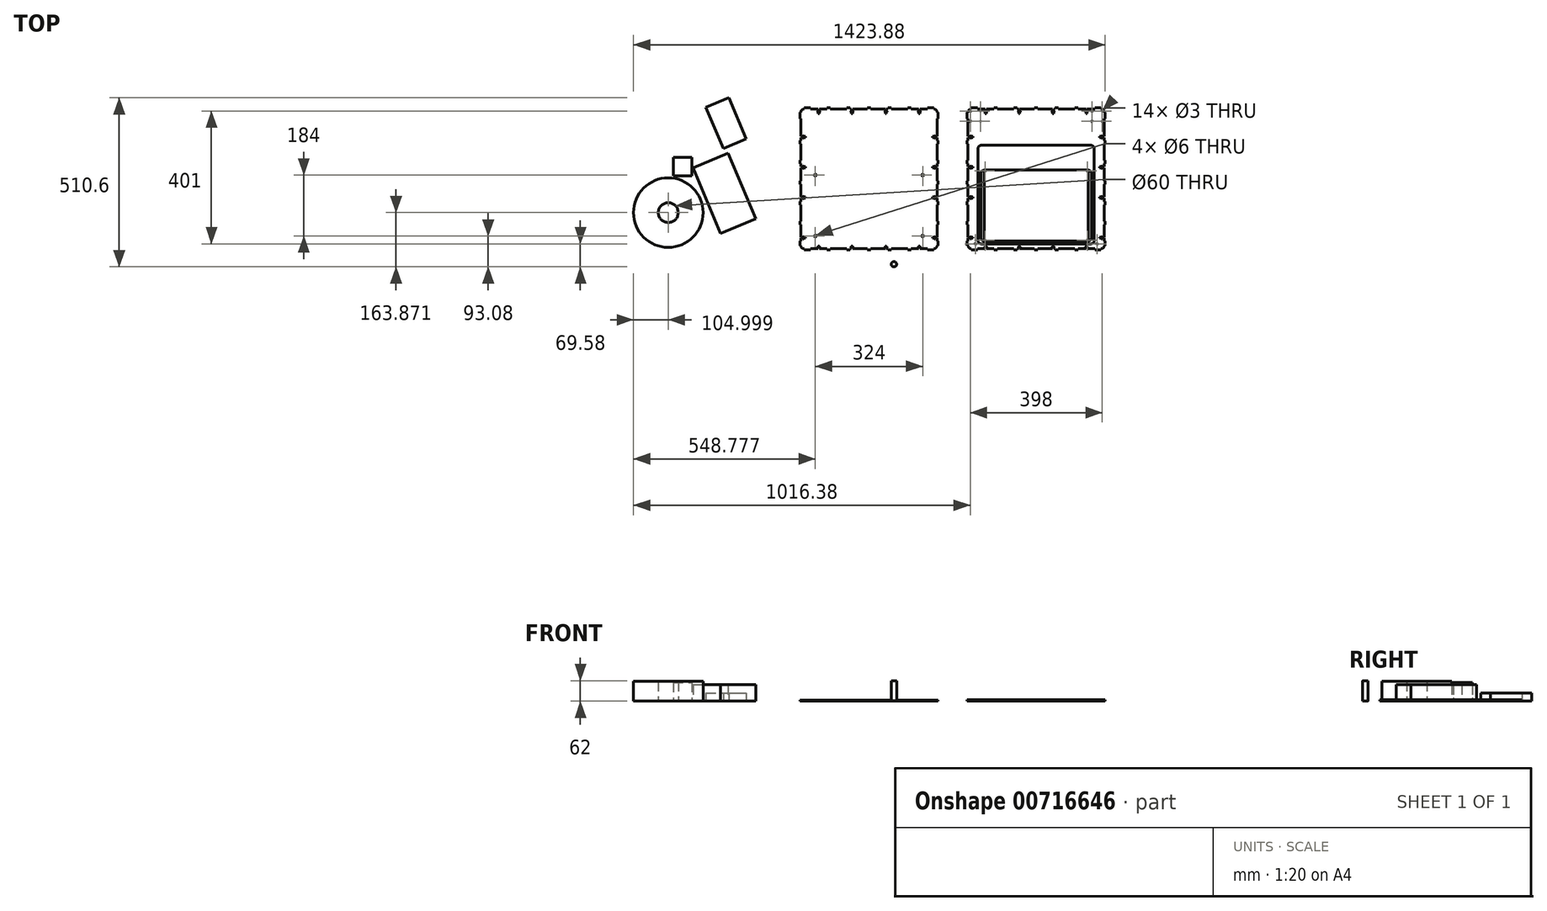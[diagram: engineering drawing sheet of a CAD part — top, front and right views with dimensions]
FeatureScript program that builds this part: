
annotation { "Feature Type Name" : "Feature", "Feature Type Description" : "" }
export const myFeature = defineFeature(function(context is Context, id is Id, definition is map)
    precondition{}
    {
        {
            var Q0;
            Q0=qCreatedBy(makeId("Top.planeOp"),FACE);
            var sketch = newSketch(context, id + "F0", { "sketchPlane" : qUnion([Q0])});
            skCircle(sketch, "E0", {"center": v(-429.2, -257.83) * mm, "radius": 8 * mm});
            skSolve(sketch);
        }
        {
            var Q0;
            Q0=makeQuery(id+"F0.imprint","IMPRINT",FACE,{"disambiguationData":[TD([[makeQuery(id+"F0.imprint","IMPRINT",EDGE,{"derivedFrom":sQuery(id+"F0.wireOp",EDGE,"E0")}),1.0]])]});
            extrude(context, id + "F1", {"entities" : qUnion([Q0]), "depth" : 62 * mm, "offsetDistance" : 25 * mm});
        }
        {
            var Q0;
            Q0=qCreatedBy(makeId("Top.planeOp"),FACE);
            var sketch = newSketch(context, id + "F2", { "sketchPlane" : qUnion([Q0])});
            skLineSegment(sketch, "E1", {"start": v(49.3, -211.25) * mm, "end": v(5, -211.25) * mm});
            skLineSegment(sketch, "E2", {"start": v(49.3, -208.35) * mm, "end": v(49.3, -211.25) * mm});
            skLineSegment(sketch, "E3", {"start": v(49.3, -208.35) * mm, "end": v(47.8, -208.35) * mm});
            skLineSegment(sketch, "E4", {"start": v(47.8, -205.75) * mm, "end": v(47.8, -208.35) * mm});
            skLineSegment(sketch, "E5", {"start": v(49.3, -205.75) * mm, "end": v(47.8, -205.75) * mm});
            skLineSegment(sketch, "E6", {"start": v(49.3, -202.75) * mm, "end": v(49.3, -205.75) * mm});
            skLineSegment(sketch, "E7", {"start": v(52.7, -202.75) * mm, "end": v(49.3, -202.75) * mm});
            skLineSegment(sketch, "E8", {"start": v(52.7, -205.75) * mm, "end": v(52.7, -202.75) * mm});
            skLineSegment(sketch, "E9", {"start": v(54.2, -205.75) * mm, "end": v(52.7, -205.75) * mm});
            skLineSegment(sketch, "E10", {"start": v(54.2, -208.35) * mm, "end": v(54.2, -205.75) * mm});
            skLineSegment(sketch, "E11", {"start": v(54.2, -208.35) * mm, "end": v(52.7, -208.35) * mm});
            skLineSegment(sketch, "E12", {"start": v(52.7, -211.25) * mm, "end": v(52.7, -208.35) * mm});
            skLineSegment(sketch, "E13", {"start": v(57, -211.25) * mm, "end": v(52.7, -211.25) * mm});
            skLineSegment(sketch, "E14", {"start": v(57, -214.25) * mm, "end": v(57, -211.25) * mm});
            skLineSegment(sketch, "E15", {"start": v(67, -214.25) * mm, "end": v(57, -214.25) * mm});
            skLineSegment(sketch, "E16", {"start": v(67, -211.25) * mm, "end": v(67, -214.25) * mm});
            skLineSegment(sketch, "E17", {"start": v(117, -211.25) * mm, "end": v(67, -211.25) * mm});
            skLineSegment(sketch, "E18", {"start": v(117, -214.25) * mm, "end": v(117, -211.25) * mm});
            skLineSegment(sketch, "E19", {"start": v(127, -214.25) * mm, "end": v(117, -214.25) * mm});
            skLineSegment(sketch, "E20", {"start": v(127, -211.25) * mm, "end": v(127, -214.25) * mm});
            skLineSegment(sketch, "E21", {"start": v(150.3, -211.25) * mm, "end": v(127, -211.25) * mm});
            skLineSegment(sketch, "E22", {"start": v(150.3, -208.35) * mm, "end": v(150.3, -211.25) * mm});
            skLineSegment(sketch, "E23", {"start": v(148.8, -208.35) * mm, "end": v(150.3, -208.35) * mm});
            skLineSegment(sketch, "E24", {"start": v(148.8, -205.75) * mm, "end": v(148.8, -208.35) * mm});
            skLineSegment(sketch, "E25", {"start": v(150.3, -205.75) * mm, "end": v(148.8, -205.75) * mm});
            skLineSegment(sketch, "E26", {"start": v(150.3, -202.75) * mm, "end": v(150.3, -205.75) * mm});
            skLineSegment(sketch, "E27", {"start": v(153.7, -202.75) * mm, "end": v(150.3, -202.75) * mm});
            skLineSegment(sketch, "E28", {"start": v(153.7, -205.75) * mm, "end": v(153.7, -202.75) * mm});
            skLineSegment(sketch, "E29", {"start": v(155.2, -205.75) * mm, "end": v(153.7, -205.75) * mm});
            skLineSegment(sketch, "E30", {"start": v(155.2, -208.35) * mm, "end": v(155.2, -205.75) * mm});
            skLineSegment(sketch, "E31", {"start": v(153.7, -208.35) * mm, "end": v(155.2, -208.35) * mm});
            skLineSegment(sketch, "E32", {"start": v(153.7, -211.25) * mm, "end": v(153.7, -208.35) * mm});
            skLineSegment(sketch, "E33", {"start": v(177, -211.25) * mm, "end": v(153.7, -211.25) * mm});
            skLineSegment(sketch, "E34", {"start": v(177, -214.25) * mm, "end": v(177, -211.25) * mm});
            skLineSegment(sketch, "E35", {"start": v(195.5, -214.25) * mm, "end": v(177, -214.25) * mm});
            skLineSegment(sketch, "E36", {"start": v(195.5, -211.25) * mm, "end": v(195.5, -214.25) * mm});
            skArc(sketch, "E37", {"start": v(205.5, -201.25) * mm, "mid": v(202.57, -208.32) * mm, "end": v(195.5, -211.25) * mm});
            skLineSegment(sketch, "E38", {"start": v(208.5, -201.25) * mm, "end": v(205.5, -201.25) * mm});
            skLineSegment(sketch, "E39", {"start": v(208.5, -188.25) * mm, "end": v(208.5, -201.25) * mm});
            skLineSegment(sketch, "E40", {"start": v(205.5, -188.25) * mm, "end": v(208.5, -188.25) * mm});
            skLineSegment(sketch, "E41", {"start": v(205.5, -179.45) * mm, "end": v(205.5, -188.25) * mm});
            skLineSegment(sketch, "E42", {"start": v(199.1, -179.45) * mm, "end": v(205.5, -179.45) * mm});
            skLineSegment(sketch, "E43", {"start": v(199.1, -180.95) * mm, "end": v(199.1, -179.45) * mm});
            skLineSegment(sketch, "E44", {"start": v(196.5, -180.95) * mm, "end": v(199.1, -180.95) * mm});
            skLineSegment(sketch, "E45", {"start": v(196.5, -179.45) * mm, "end": v(196.5, -180.95) * mm});
            skLineSegment(sketch, "E46", {"start": v(191.5, -179.45) * mm, "end": v(196.5, -179.45) * mm});
            skLineSegment(sketch, "E47", {"start": v(191.5, -176.05) * mm, "end": v(191.5, -179.45) * mm});
            skLineSegment(sketch, "E48", {"start": v(196.5, -176.05) * mm, "end": v(191.5, -176.05) * mm});
            skLineSegment(sketch, "E49", {"start": v(196.5, -174.55) * mm, "end": v(196.5, -176.05) * mm});
            skLineSegment(sketch, "E50", {"start": v(199.1, -174.55) * mm, "end": v(196.5, -174.55) * mm});
            skLineSegment(sketch, "E51", {"start": v(199.1, -176.05) * mm, "end": v(199.1, -174.55) * mm});
            skLineSegment(sketch, "E52", {"start": v(205.5, -176.05) * mm, "end": v(199.1, -176.05) * mm});
            skLineSegment(sketch, "E53", {"start": v(205.5, -138.25) * mm, "end": v(205.5, -176.05) * mm});
            skLineSegment(sketch, "E54", {"start": v(208.5, -138.25) * mm, "end": v(205.5, -138.25) * mm});
            skLineSegment(sketch, "E55", {"start": v(208.5, -128.25) * mm, "end": v(208.5, -138.25) * mm});
            skLineSegment(sketch, "E56", {"start": v(205.5, -128.25) * mm, "end": v(208.5, -128.25) * mm});
            skLineSegment(sketch, "E57", {"start": v(205.5, -78.25) * mm, "end": v(205.5, -128.25) * mm});
            skLineSegment(sketch, "E58", {"start": v(208.5, -78.25) * mm, "end": v(205.5, -78.25) * mm});
            skLineSegment(sketch, "E59", {"start": v(208.5, -68.25) * mm, "end": v(208.5, -78.25) * mm});
            skLineSegment(sketch, "E60", {"start": v(205.5, -68.25) * mm, "end": v(208.5, -68.25) * mm});
            skLineSegment(sketch, "E61", {"start": v(205.5, -58.45) * mm, "end": v(205.5, -68.25) * mm});
            skLineSegment(sketch, "E62", {"start": v(199.1, -58.45) * mm, "end": v(205.5, -58.45) * mm});
            skLineSegment(sketch, "E63", {"start": v(199.1, -59.95) * mm, "end": v(199.1, -58.45) * mm});
            skLineSegment(sketch, "E64", {"start": v(196.5, -59.95) * mm, "end": v(199.1, -59.95) * mm});
            skLineSegment(sketch, "E65", {"start": v(196.5, -58.45) * mm, "end": v(196.5, -59.95) * mm});
            skLineSegment(sketch, "E66", {"start": v(191.5, -58.45) * mm, "end": v(196.5, -58.45) * mm});
            skLineSegment(sketch, "E67", {"start": v(191.5, -55.05) * mm, "end": v(191.5, -58.45) * mm});
            skLineSegment(sketch, "E68", {"start": v(196.5, -55.05) * mm, "end": v(191.5, -55.05) * mm});
            skLineSegment(sketch, "E69", {"start": v(196.5, -53.55) * mm, "end": v(196.5, -55.05) * mm});
            skLineSegment(sketch, "E70", {"start": v(199.1, -53.55) * mm, "end": v(196.5, -53.55) * mm});
            skLineSegment(sketch, "E71", {"start": v(199.1, -55.05) * mm, "end": v(199.1, -53.55) * mm});
            skLineSegment(sketch, "E72", {"start": v(205.5, -55.05) * mm, "end": v(199.1, -55.05) * mm});
            skLineSegment(sketch, "E73", {"start": v(205.5, -16.25) * mm, "end": v(205.5, -55.05) * mm});
            skLineSegment(sketch, "E74", {"start": v(208.5, -16.25) * mm, "end": v(205.5, -16.25) * mm});
            skLineSegment(sketch, "E75", {"start": v(208.5, -6.25) * mm, "end": v(208.5, -16.25) * mm});
            skLineSegment(sketch, "E76", {"start": v(205.5, -6.25) * mm, "end": v(208.5, -6.25) * mm});
            skLineSegment(sketch, "E77", {"start": v(205.5, 33.55) * mm, "end": v(205.5, -6.25) * mm});
            skLineSegment(sketch, "E78", {"start": v(199.1, 33.55) * mm, "end": v(205.5, 33.55) * mm});
            skLineSegment(sketch, "E79", {"start": v(199.1, 33.55) * mm, "end": v(199.1, 32.05) * mm});
            skLineSegment(sketch, "E80", {"start": v(196.5, 32.05) * mm, "end": v(199.1, 32.05) * mm});
            skLineSegment(sketch, "E81", {"start": v(196.5, 33.55) * mm, "end": v(196.5, 32.05) * mm});
            skLineSegment(sketch, "E82", {"start": v(191.5, 33.55) * mm, "end": v(196.5, 33.55) * mm});
            skLineSegment(sketch, "E83", {"start": v(191.5, 36.95) * mm, "end": v(191.5, 33.55) * mm});
            skLineSegment(sketch, "E84", {"start": v(196.5, 36.95) * mm, "end": v(191.5, 36.95) * mm});
            skLineSegment(sketch, "E85", {"start": v(196.5, 38.45) * mm, "end": v(196.5, 36.95) * mm});
            skLineSegment(sketch, "E86", {"start": v(199.1, 38.45) * mm, "end": v(196.5, 38.45) * mm});
            skLineSegment(sketch, "E87", {"start": v(199.1, 38.45) * mm, "end": v(199.1, 36.95) * mm});
            skLineSegment(sketch, "E88", {"start": v(205.5, 36.95) * mm, "end": v(199.1, 36.95) * mm});
            skLineSegment(sketch, "E89", {"start": v(205.5, 45.75) * mm, "end": v(205.5, 36.95) * mm});
            skLineSegment(sketch, "E90", {"start": v(208.5, 45.75) * mm, "end": v(205.5, 45.75) * mm});
            skLineSegment(sketch, "E91", {"start": v(208.5, 55.75) * mm, "end": v(208.5, 45.75) * mm});
            skLineSegment(sketch, "E92", {"start": v(205.5, 55.75) * mm, "end": v(208.5, 55.75) * mm});
            skLineSegment(sketch, "E93", {"start": v(205.5, 105.75) * mm, "end": v(205.5, 55.75) * mm});
            skLineSegment(sketch, "E94", {"start": v(208.5, 105.75) * mm, "end": v(205.5, 105.75) * mm});
            skLineSegment(sketch, "E95", {"start": v(208.5, 115.75) * mm, "end": v(208.5, 105.75) * mm});
            skLineSegment(sketch, "E96", {"start": v(205.5, 115.75) * mm, "end": v(208.5, 115.75) * mm});
            skLineSegment(sketch, "E97", {"start": v(205.5, 124.55) * mm, "end": v(205.5, 115.75) * mm});
            skLineSegment(sketch, "E98", {"start": v(199.1, 124.55) * mm, "end": v(205.5, 124.55) * mm});
            skLineSegment(sketch, "E99", {"start": v(199.1, 123.05) * mm, "end": v(199.1, 124.55) * mm});
            skLineSegment(sketch, "E100", {"start": v(196.5, 123.05) * mm, "end": v(199.1, 123.05) * mm});
            skLineSegment(sketch, "E101", {"start": v(196.5, 124.55) * mm, "end": v(196.5, 123.05) * mm});
            skLineSegment(sketch, "E102", {"start": v(191.5, 124.55) * mm, "end": v(196.5, 124.55) * mm});
            skLineSegment(sketch, "E103", {"start": v(191.5, 127.95) * mm, "end": v(191.5, 124.55) * mm});
            skLineSegment(sketch, "E104", {"start": v(196.5, 127.95) * mm, "end": v(191.5, 127.95) * mm});
            skLineSegment(sketch, "E105", {"start": v(196.5, 129.45) * mm, "end": v(196.5, 127.95) * mm});
            skLineSegment(sketch, "E106", {"start": v(199.1, 129.45) * mm, "end": v(196.5, 129.45) * mm});
            skLineSegment(sketch, "E107", {"start": v(199.1, 127.95) * mm, "end": v(199.1, 129.45) * mm});
            skLineSegment(sketch, "E108", {"start": v(205.5, 127.95) * mm, "end": v(199.1, 127.95) * mm});
            skLineSegment(sketch, "E109", {"start": v(205.5, 181.25) * mm, "end": v(205.5, 127.95) * mm});
            skLineSegment(sketch, "E110", {"start": v(208.5, 181.25) * mm, "end": v(205.5, 181.25) * mm});
            skLineSegment(sketch, "E111", {"start": v(208.5, 201.25) * mm, "end": v(208.5, 181.25) * mm});
            skLineSegment(sketch, "E112", {"start": v(205.5, 201.25) * mm, "end": v(208.5, 201.25) * mm});
            skArc(sketch, "E113", {"start": v(195.5, 211.25) * mm, "mid": v(202.57, 208.32) * mm, "end": v(205.5, 201.25) * mm});
            skLineSegment(sketch, "E114", {"start": v(195.5, 214.25) * mm, "end": v(195.5, 211.25) * mm});
            skLineSegment(sketch, "E115", {"start": v(177, 214.25) * mm, "end": v(195.5, 214.25) * mm});
            skLineSegment(sketch, "E116", {"start": v(177, 211.25) * mm, "end": v(177, 214.25) * mm});
            skLineSegment(sketch, "E117", {"start": v(153.7, 211.25) * mm, "end": v(177, 211.25) * mm});
            skLineSegment(sketch, "E118", {"start": v(153.7, 204.85) * mm, "end": v(153.7, 211.25) * mm});
            skLineSegment(sketch, "E119", {"start": v(155.2, 204.85) * mm, "end": v(153.7, 204.85) * mm});
            skLineSegment(sketch, "E120", {"start": v(155.2, 202.25) * mm, "end": v(155.2, 204.85) * mm});
            skLineSegment(sketch, "E121", {"start": v(153.7, 202.25) * mm, "end": v(155.2, 202.25) * mm});
            skLineSegment(sketch, "E122", {"start": v(153.7, 197.25) * mm, "end": v(153.7, 202.25) * mm});
            skLineSegment(sketch, "E123", {"start": v(150.3, 197.25) * mm, "end": v(153.7, 197.25) * mm});
            skLineSegment(sketch, "E124", {"start": v(150.3, 202.25) * mm, "end": v(150.3, 197.25) * mm});
            skLineSegment(sketch, "E125", {"start": v(148.8, 202.25) * mm, "end": v(150.3, 202.25) * mm});
            skLineSegment(sketch, "E126", {"start": v(148.8, 204.85) * mm, "end": v(148.8, 202.25) * mm});
            skLineSegment(sketch, "E127", {"start": v(150.3, 204.85) * mm, "end": v(148.8, 204.85) * mm});
            skLineSegment(sketch, "E128", {"start": v(150.3, 211.25) * mm, "end": v(150.3, 204.85) * mm});
            skLineSegment(sketch, "E129", {"start": v(127, 211.25) * mm, "end": v(150.3, 211.25) * mm});
            skLineSegment(sketch, "E130", {"start": v(127, 214.25) * mm, "end": v(127, 211.25) * mm});
            skLineSegment(sketch, "E131", {"start": v(117, 214.25) * mm, "end": v(127, 214.25) * mm});
            skLineSegment(sketch, "E132", {"start": v(117, 211.25) * mm, "end": v(117, 214.25) * mm});
            skLineSegment(sketch, "E133", {"start": v(67, 211.25) * mm, "end": v(117, 211.25) * mm});
            skLineSegment(sketch, "E134", {"start": v(67, 214.25) * mm, "end": v(67, 211.25) * mm});
            skLineSegment(sketch, "E135", {"start": v(57, 214.25) * mm, "end": v(67, 214.25) * mm});
            skLineSegment(sketch, "E136", {"start": v(57, 211.25) * mm, "end": v(57, 214.25) * mm});
            skLineSegment(sketch, "E137", {"start": v(52.7, 211.25) * mm, "end": v(57, 211.25) * mm});
            skLineSegment(sketch, "E138", {"start": v(52.7, 204.85) * mm, "end": v(52.7, 211.25) * mm});
            skLineSegment(sketch, "E139", {"start": v(54.2, 204.85) * mm, "end": v(52.7, 204.85) * mm});
            skLineSegment(sketch, "E140", {"start": v(54.2, 202.25) * mm, "end": v(54.2, 204.85) * mm});
            skLineSegment(sketch, "E141", {"start": v(54.2, 202.25) * mm, "end": v(52.7, 202.25) * mm});
            skLineSegment(sketch, "E142", {"start": v(52.7, 197.25) * mm, "end": v(52.7, 202.25) * mm});
            skLineSegment(sketch, "E143", {"start": v(49.3, 197.25) * mm, "end": v(52.7, 197.25) * mm});
            skLineSegment(sketch, "E144", {"start": v(49.3, 202.25) * mm, "end": v(49.3, 197.25) * mm});
            skLineSegment(sketch, "E145", {"start": v(49.3, 202.25) * mm, "end": v(47.8, 202.25) * mm});
            skLineSegment(sketch, "E146", {"start": v(47.8, 204.85) * mm, "end": v(47.8, 202.25) * mm});
            skLineSegment(sketch, "E147", {"start": v(49.3, 204.85) * mm, "end": v(47.8, 204.85) * mm});
            skLineSegment(sketch, "E148", {"start": v(49.3, 211.25) * mm, "end": v(49.3, 204.85) * mm});
            skLineSegment(sketch, "E149", {"start": v(5, 211.25) * mm, "end": v(49.3, 211.25) * mm});
            skLineSegment(sketch, "E150", {"start": v(5, 214.25) * mm, "end": v(5, 211.25) * mm});
            skLineSegment(sketch, "E151", {"start": v(-5, 214.25) * mm, "end": v(5, 214.25) * mm});
            skLineSegment(sketch, "E152", {"start": v(-5, 211.25) * mm, "end": v(-5, 214.25) * mm});
            skLineSegment(sketch, "E153", {"start": v(-49.3, 211.25) * mm, "end": v(-5, 211.25) * mm});
            skLineSegment(sketch, "E154", {"start": v(-49.3, 204.85) * mm, "end": v(-49.3, 211.25) * mm});
            skLineSegment(sketch, "E155", {"start": v(-49.3, 204.85) * mm, "end": v(-47.8, 204.85) * mm});
            skLineSegment(sketch, "E156", {"start": v(-47.8, 202.25) * mm, "end": v(-47.8, 204.85) * mm});
            skLineSegment(sketch, "E157", {"start": v(-49.3, 202.25) * mm, "end": v(-47.8, 202.25) * mm});
            skLineSegment(sketch, "E158", {"start": v(-49.3, 197.25) * mm, "end": v(-49.3, 202.25) * mm});
            skLineSegment(sketch, "E159", {"start": v(-52.7, 197.25) * mm, "end": v(-49.3, 197.25) * mm});
            skLineSegment(sketch, "E160", {"start": v(-52.7, 202.25) * mm, "end": v(-52.7, 197.25) * mm});
            skLineSegment(sketch, "E161", {"start": v(-54.2, 202.25) * mm, "end": v(-52.7, 202.25) * mm});
            skLineSegment(sketch, "E162", {"start": v(-54.2, 204.85) * mm, "end": v(-54.2, 202.25) * mm});
            skLineSegment(sketch, "E163", {"start": v(-54.2, 204.85) * mm, "end": v(-52.7, 204.85) * mm});
            skLineSegment(sketch, "E164", {"start": v(-52.7, 211.25) * mm, "end": v(-52.7, 204.85) * mm});
            skLineSegment(sketch, "E165", {"start": v(-57, 211.25) * mm, "end": v(-52.7, 211.25) * mm});
            skLineSegment(sketch, "E166", {"start": v(-57, 214.25) * mm, "end": v(-57, 211.25) * mm});
            skLineSegment(sketch, "E167", {"start": v(-67, 214.25) * mm, "end": v(-57, 214.25) * mm});
            skLineSegment(sketch, "E168", {"start": v(-67, 211.25) * mm, "end": v(-67, 214.25) * mm});
            skLineSegment(sketch, "E169", {"start": v(-117, 211.25) * mm, "end": v(-67, 211.25) * mm});
            skLineSegment(sketch, "E170", {"start": v(-117, 214.25) * mm, "end": v(-117, 211.25) * mm});
            skLineSegment(sketch, "E171", {"start": v(-127, 214.25) * mm, "end": v(-117, 214.25) * mm});
            skLineSegment(sketch, "E172", {"start": v(-127, 211.25) * mm, "end": v(-127, 214.25) * mm});
            skLineSegment(sketch, "E173", {"start": v(-150.3, 211.25) * mm, "end": v(-127, 211.25) * mm});
            skLineSegment(sketch, "E174", {"start": v(-150.3, 204.85) * mm, "end": v(-150.3, 211.25) * mm});
            skLineSegment(sketch, "E175", {"start": v(-148.8, 204.85) * mm, "end": v(-150.3, 204.85) * mm});
            skLineSegment(sketch, "E176", {"start": v(-148.8, 202.25) * mm, "end": v(-148.8, 204.85) * mm});
            skLineSegment(sketch, "E177", {"start": v(-150.3, 202.25) * mm, "end": v(-148.8, 202.25) * mm});
            skLineSegment(sketch, "E178", {"start": v(-150.3, 197.25) * mm, "end": v(-150.3, 202.25) * mm});
            skLineSegment(sketch, "E179", {"start": v(-153.7, 197.25) * mm, "end": v(-150.3, 197.25) * mm});
            skLineSegment(sketch, "E180", {"start": v(-153.7, 202.25) * mm, "end": v(-153.7, 197.25) * mm});
            skLineSegment(sketch, "E181", {"start": v(-155.2, 202.25) * mm, "end": v(-153.7, 202.25) * mm});
            skLineSegment(sketch, "E182", {"start": v(-155.2, 204.85) * mm, "end": v(-155.2, 202.25) * mm});
            skLineSegment(sketch, "E183", {"start": v(-153.7, 204.85) * mm, "end": v(-155.2, 204.85) * mm});
            skLineSegment(sketch, "E184", {"start": v(-153.7, 211.25) * mm, "end": v(-153.7, 204.85) * mm});
            skLineSegment(sketch, "E185", {"start": v(-177, 211.25) * mm, "end": v(-153.7, 211.25) * mm});
            skLineSegment(sketch, "E186", {"start": v(-177, 214.25) * mm, "end": v(-177, 211.25) * mm});
            skLineSegment(sketch, "E187", {"start": v(-195.5, 214.25) * mm, "end": v(-177, 214.25) * mm});
            skLineSegment(sketch, "E188", {"start": v(-195.5, 211.25) * mm, "end": v(-195.5, 214.25) * mm});
            skArc(sketch, "E189", {"start": v(-205.5, 201.25) * mm, "mid": v(-202.57, 208.32) * mm, "end": v(-195.5, 211.25) * mm});
            skLineSegment(sketch, "E190", {"start": v(-208.5, 201.25) * mm, "end": v(-205.5, 201.25) * mm});
            skLineSegment(sketch, "E191", {"start": v(-208.5, 181.25) * mm, "end": v(-208.5, 201.25) * mm});
            skLineSegment(sketch, "E192", {"start": v(-205.5, 181.25) * mm, "end": v(-208.5, 181.25) * mm});
            skLineSegment(sketch, "E193", {"start": v(-205.5, 127.95) * mm, "end": v(-205.5, 181.25) * mm});
            skLineSegment(sketch, "E194", {"start": v(-199.1, 127.95) * mm, "end": v(-205.5, 127.95) * mm});
            skLineSegment(sketch, "E195", {"start": v(-199.1, 129.45) * mm, "end": v(-199.1, 127.95) * mm});
            skLineSegment(sketch, "E196", {"start": v(-196.5, 129.45) * mm, "end": v(-199.1, 129.45) * mm});
            skLineSegment(sketch, "E197", {"start": v(-196.5, 127.95) * mm, "end": v(-196.5, 129.45) * mm});
            skLineSegment(sketch, "E198", {"start": v(-191.5, 127.95) * mm, "end": v(-196.5, 127.95) * mm});
            skLineSegment(sketch, "E199", {"start": v(-191.5, 124.55) * mm, "end": v(-191.5, 127.95) * mm});
            skLineSegment(sketch, "E200", {"start": v(-196.5, 124.55) * mm, "end": v(-191.5, 124.55) * mm});
            skLineSegment(sketch, "E201", {"start": v(-196.5, 123.05) * mm, "end": v(-196.5, 124.55) * mm});
            skLineSegment(sketch, "E202", {"start": v(-199.1, 123.05) * mm, "end": v(-196.5, 123.05) * mm});
            skLineSegment(sketch, "E203", {"start": v(-199.1, 124.55) * mm, "end": v(-199.1, 123.05) * mm});
            skLineSegment(sketch, "E204", {"start": v(-205.5, 124.55) * mm, "end": v(-199.1, 124.55) * mm});
            skLineSegment(sketch, "E205", {"start": v(-205.5, 115.75) * mm, "end": v(-205.5, 124.55) * mm});
            skLineSegment(sketch, "E206", {"start": v(-208.5, 115.75) * mm, "end": v(-205.5, 115.75) * mm});
            skLineSegment(sketch, "E207", {"start": v(-208.5, 105.75) * mm, "end": v(-208.5, 115.75) * mm});
            skLineSegment(sketch, "E208", {"start": v(-205.5, 105.75) * mm, "end": v(-208.5, 105.75) * mm});
            skLineSegment(sketch, "E209", {"start": v(-205.5, 55.75) * mm, "end": v(-205.5, 105.75) * mm});
            skLineSegment(sketch, "E210", {"start": v(-208.5, 55.75) * mm, "end": v(-205.5, 55.75) * mm});
            skLineSegment(sketch, "E211", {"start": v(-208.5, 45.75) * mm, "end": v(-208.5, 55.75) * mm});
            skLineSegment(sketch, "E212", {"start": v(-205.5, 45.75) * mm, "end": v(-208.5, 45.75) * mm});
            skLineSegment(sketch, "E213", {"start": v(-205.5, 36.95) * mm, "end": v(-205.5, 45.75) * mm});
            skLineSegment(sketch, "E214", {"start": v(-199.1, 36.95) * mm, "end": v(-205.5, 36.95) * mm});
            skLineSegment(sketch, "E215", {"start": v(-199.1, 38.45) * mm, "end": v(-199.1, 36.95) * mm});
            skLineSegment(sketch, "E216", {"start": v(-196.5, 38.45) * mm, "end": v(-199.1, 38.45) * mm});
            skLineSegment(sketch, "E217", {"start": v(-196.5, 38.45) * mm, "end": v(-196.5, 36.95) * mm});
            skLineSegment(sketch, "E218", {"start": v(-191.5, 36.95) * mm, "end": v(-196.5, 36.95) * mm});
            skLineSegment(sketch, "E219", {"start": v(-191.5, 33.55) * mm, "end": v(-191.5, 36.95) * mm});
            skLineSegment(sketch, "E220", {"start": v(-196.5, 33.55) * mm, "end": v(-191.5, 33.55) * mm});
            skLineSegment(sketch, "E221", {"start": v(-196.5, 33.55) * mm, "end": v(-196.5, 32.05) * mm});
            skLineSegment(sketch, "E222", {"start": v(-199.1, 32.05) * mm, "end": v(-196.5, 32.05) * mm});
            skLineSegment(sketch, "E223", {"start": v(-199.1, 33.55) * mm, "end": v(-199.1, 32.05) * mm});
            skLineSegment(sketch, "E224", {"start": v(-205.5, 33.55) * mm, "end": v(-199.1, 33.55) * mm});
            skLineSegment(sketch, "E225", {"start": v(-205.5, -6.25) * mm, "end": v(-205.5, 33.55) * mm});
            skLineSegment(sketch, "E226", {"start": v(-208.5, -6.25) * mm, "end": v(-205.5, -6.25) * mm});
            skLineSegment(sketch, "E227", {"start": v(-208.5, -16.25) * mm, "end": v(-208.5, -6.25) * mm});
            skLineSegment(sketch, "E228", {"start": v(-205.5, -16.25) * mm, "end": v(-208.5, -16.25) * mm});
            skLineSegment(sketch, "E229", {"start": v(-205.5, -55.05) * mm, "end": v(-205.5, -16.25) * mm});
            skLineSegment(sketch, "E230", {"start": v(-199.1, -55.05) * mm, "end": v(-205.5, -55.05) * mm});
            skLineSegment(sketch, "E231", {"start": v(-199.1, -53.55) * mm, "end": v(-199.1, -55.05) * mm});
            skLineSegment(sketch, "E232", {"start": v(-196.5, -53.55) * mm, "end": v(-199.1, -53.55) * mm});
            skLineSegment(sketch, "E233", {"start": v(-196.5, -55.05) * mm, "end": v(-196.5, -53.55) * mm});
            skLineSegment(sketch, "E234", {"start": v(-191.5, -55.05) * mm, "end": v(-196.5, -55.05) * mm});
            skLineSegment(sketch, "E235", {"start": v(-191.5, -58.45) * mm, "end": v(-191.5, -55.05) * mm});
            skLineSegment(sketch, "E236", {"start": v(-196.5, -58.45) * mm, "end": v(-191.5, -58.45) * mm});
            skLineSegment(sketch, "E237", {"start": v(-196.5, -59.95) * mm, "end": v(-196.5, -58.45) * mm});
            skLineSegment(sketch, "E238", {"start": v(-199.1, -59.95) * mm, "end": v(-196.5, -59.95) * mm});
            skLineSegment(sketch, "E239", {"start": v(-199.1, -58.45) * mm, "end": v(-199.1, -59.95) * mm});
            skLineSegment(sketch, "E240", {"start": v(-205.5, -58.45) * mm, "end": v(-199.1, -58.45) * mm});
            skLineSegment(sketch, "E241", {"start": v(-205.5, -68.25) * mm, "end": v(-205.5, -58.45) * mm});
            skLineSegment(sketch, "E242", {"start": v(-208.5, -68.25) * mm, "end": v(-205.5, -68.25) * mm});
            skLineSegment(sketch, "E243", {"start": v(-208.5, -78.25) * mm, "end": v(-208.5, -68.25) * mm});
            skLineSegment(sketch, "E244", {"start": v(-205.5, -78.25) * mm, "end": v(-208.5, -78.25) * mm});
            skLineSegment(sketch, "E245", {"start": v(-205.5, -128.25) * mm, "end": v(-205.5, -78.25) * mm});
            skLineSegment(sketch, "E246", {"start": v(-208.5, -128.25) * mm, "end": v(-205.5, -128.25) * mm});
            skLineSegment(sketch, "E247", {"start": v(-208.5, -138.25) * mm, "end": v(-208.5, -128.25) * mm});
            skLineSegment(sketch, "E248", {"start": v(-205.5, -138.25) * mm, "end": v(-208.5, -138.25) * mm});
            skLineSegment(sketch, "E249", {"start": v(-205.5, -176.05) * mm, "end": v(-205.5, -138.25) * mm});
            skLineSegment(sketch, "E250", {"start": v(-199.1, -176.05) * mm, "end": v(-205.5, -176.05) * mm});
            skLineSegment(sketch, "E251", {"start": v(-199.1, -174.55) * mm, "end": v(-199.1, -176.05) * mm});
            skLineSegment(sketch, "E252", {"start": v(-196.5, -174.55) * mm, "end": v(-199.1, -174.55) * mm});
            skLineSegment(sketch, "E253", {"start": v(-196.5, -176.05) * mm, "end": v(-196.5, -174.55) * mm});
            skLineSegment(sketch, "E254", {"start": v(-191.5, -176.05) * mm, "end": v(-196.5, -176.05) * mm});
            skLineSegment(sketch, "E255", {"start": v(-191.5, -179.45) * mm, "end": v(-191.5, -176.05) * mm});
            skLineSegment(sketch, "E256", {"start": v(-196.5, -179.45) * mm, "end": v(-191.5, -179.45) * mm});
            skLineSegment(sketch, "E257", {"start": v(-196.5, -180.95) * mm, "end": v(-196.5, -179.45) * mm});
            skLineSegment(sketch, "E258", {"start": v(-199.1, -180.95) * mm, "end": v(-196.5, -180.95) * mm});
            skLineSegment(sketch, "E259", {"start": v(-199.1, -179.45) * mm, "end": v(-199.1, -180.95) * mm});
            skLineSegment(sketch, "E260", {"start": v(-205.5, -179.45) * mm, "end": v(-199.1, -179.45) * mm});
            skLineSegment(sketch, "E261", {"start": v(-205.5, -188.25) * mm, "end": v(-205.5, -179.45) * mm});
            skLineSegment(sketch, "E262", {"start": v(-208.5, -188.25) * mm, "end": v(-205.5, -188.25) * mm});
            skLineSegment(sketch, "E263", {"start": v(-208.5, -201.25) * mm, "end": v(-208.5, -188.25) * mm});
            skLineSegment(sketch, "E264", {"start": v(-205.5, -201.25) * mm, "end": v(-208.5, -201.25) * mm});
            skArc(sketch, "E265", {"start": v(-205.5, -201.25) * mm, "mid": v(-202.57, -208.32) * mm, "end": v(-195.5, -211.25) * mm});
            skLineSegment(sketch, "E266", {"start": v(-195.5, -214.25) * mm, "end": v(-195.5, -211.25) * mm});
            skLineSegment(sketch, "E267", {"start": v(-177, -214.25) * mm, "end": v(-195.5, -214.25) * mm});
            skLineSegment(sketch, "E268", {"start": v(-177, -211.25) * mm, "end": v(-177, -214.25) * mm});
            skLineSegment(sketch, "E269", {"start": v(-153.7, -211.25) * mm, "end": v(-177, -211.25) * mm});
            skLineSegment(sketch, "E270", {"start": v(-153.7, -208.35) * mm, "end": v(-153.7, -211.25) * mm});
            skLineSegment(sketch, "E271", {"start": v(-155.2, -208.35) * mm, "end": v(-153.7, -208.35) * mm});
            skLineSegment(sketch, "E272", {"start": v(-155.2, -205.75) * mm, "end": v(-155.2, -208.35) * mm});
            skLineSegment(sketch, "E273", {"start": v(-153.7, -205.75) * mm, "end": v(-155.2, -205.75) * mm});
            skLineSegment(sketch, "E274", {"start": v(-153.7, -202.75) * mm, "end": v(-153.7, -205.75) * mm});
            skLineSegment(sketch, "E275", {"start": v(-150.3, -202.75) * mm, "end": v(-153.7, -202.75) * mm});
            skLineSegment(sketch, "E276", {"start": v(-150.3, -205.75) * mm, "end": v(-150.3, -202.75) * mm});
            skLineSegment(sketch, "E277", {"start": v(-148.8, -205.75) * mm, "end": v(-150.3, -205.75) * mm});
            skLineSegment(sketch, "E278", {"start": v(-148.8, -208.35) * mm, "end": v(-148.8, -205.75) * mm});
            skLineSegment(sketch, "E279", {"start": v(-150.3, -208.35) * mm, "end": v(-148.8, -208.35) * mm});
            skLineSegment(sketch, "E280", {"start": v(-150.3, -211.25) * mm, "end": v(-150.3, -208.35) * mm});
            skLineSegment(sketch, "E281", {"start": v(-127, -211.25) * mm, "end": v(-150.3, -211.25) * mm});
            skLineSegment(sketch, "E282", {"start": v(-127, -214.25) * mm, "end": v(-127, -211.25) * mm});
            skLineSegment(sketch, "E283", {"start": v(-117, -214.25) * mm, "end": v(-127, -214.25) * mm});
            skLineSegment(sketch, "E284", {"start": v(-117, -211.25) * mm, "end": v(-117, -214.25) * mm});
            skLineSegment(sketch, "E285", {"start": v(-67, -211.25) * mm, "end": v(-117, -211.25) * mm});
            skLineSegment(sketch, "E286", {"start": v(-67, -214.25) * mm, "end": v(-67, -211.25) * mm});
            skLineSegment(sketch, "E287", {"start": v(-57, -214.25) * mm, "end": v(-67, -214.25) * mm});
            skLineSegment(sketch, "E288", {"start": v(-57, -211.25) * mm, "end": v(-57, -214.25) * mm});
            skLineSegment(sketch, "E289", {"start": v(-52.7, -211.25) * mm, "end": v(-57, -211.25) * mm});
            skLineSegment(sketch, "E290", {"start": v(-52.7, -208.35) * mm, "end": v(-52.7, -211.25) * mm});
            skLineSegment(sketch, "E291", {"start": v(-54.2, -208.35) * mm, "end": v(-52.7, -208.35) * mm});
            skLineSegment(sketch, "E292", {"start": v(-54.2, -205.75) * mm, "end": v(-54.2, -208.35) * mm});
            skLineSegment(sketch, "E293", {"start": v(-54.2, -205.75) * mm, "end": v(-52.7, -205.75) * mm});
            skLineSegment(sketch, "E294", {"start": v(-52.7, -202.75) * mm, "end": v(-52.7, -205.75) * mm});
            skLineSegment(sketch, "E295", {"start": v(-49.3, -202.75) * mm, "end": v(-52.7, -202.75) * mm});
            skLineSegment(sketch, "E296", {"start": v(-49.3, -205.75) * mm, "end": v(-49.3, -202.75) * mm});
            skLineSegment(sketch, "E297", {"start": v(-49.3, -205.75) * mm, "end": v(-47.8, -205.75) * mm});
            skLineSegment(sketch, "E298", {"start": v(-47.8, -208.35) * mm, "end": v(-47.8, -205.75) * mm});
            skLineSegment(sketch, "E299", {"start": v(-49.3, -208.35) * mm, "end": v(-47.8, -208.35) * mm});
            skLineSegment(sketch, "E300", {"start": v(-49.3, -211.25) * mm, "end": v(-49.3, -208.35) * mm});
            skLineSegment(sketch, "E301", {"start": v(-5, -211.25) * mm, "end": v(-49.3, -211.25) * mm});
            skLineSegment(sketch, "E302", {"start": v(-5, -214.25) * mm, "end": v(-5, -211.25) * mm});
            skLineSegment(sketch, "E303", {"start": v(5, -214.25) * mm, "end": v(-5, -214.25) * mm});
            skLineSegment(sketch, "E304", {"start": v(5, -211.25) * mm, "end": v(5, -214.25) * mm});
            skCircle(sketch, "E305", {"center": v(-168, 173.75) * mm, "radius": 1.5 * mm});
            skCircle(sketch, "E306", {"center": v(-199, 173.75) * mm, "radius": 1.5 * mm});
            skCircle(sketch, "E307", {"center": v(-168, 204.75) * mm, "radius": 1.5 * mm});
            skCircle(sketch, "E308", {"center": v(-199, 204.75) * mm, "radius": 1.5 * mm});
            skCircle(sketch, "E309", {"center": v(168, 173.75) * mm, "radius": 1.5 * mm});
            skCircle(sketch, "E310", {"center": v(199, 173.75) * mm, "radius": 1.5 * mm});
            skCircle(sketch, "E311", {"center": v(199, 204.75) * mm, "radius": 1.5 * mm});
            skCircle(sketch, "E312", {"center": v(168, 204.75) * mm, "radius": 1.5 * mm});
            skCircle(sketch, "E313", {"center": v(183.5, -196.25) * mm, "radius": 1.5 * mm});
            skCircle(sketch, "E314", {"center": v(-183.5, -196.25) * mm, "radius": 1.5 * mm});
            skArc(sketch, "E315", {"start": v(165.5, -196.25) * mm, "mid": v(172.57, -193.32) * mm, "end": v(175.5, -186.25) * mm});
            skLineSegment(sketch, "E316", {"start": v(-165.5, -196.25) * mm, "end": v(165.5, -196.25) * mm});
            skArc(sketch, "E317", {"start": v(-165.5, -196.25) * mm, "mid": v(-172.57, -193.32) * mm, "end": v(-175.5, -186.25) * mm});
            skLineSegment(sketch, "E318", {"start": v(-175.5, 91.25) * mm, "end": v(-175.5, -186.25) * mm});
            skArc(sketch, "E319", {"start": v(-165.5, 101.25) * mm, "mid": v(-172.57, 98.32) * mm, "end": v(-175.5, 91.25) * mm});
            skLineSegment(sketch, "E320", {"start": v(165.5, 101.25) * mm, "end": v(-165.5, 101.25) * mm});
            skArc(sketch, "E321", {"start": v(165.5, 101.25) * mm, "mid": v(172.57, 98.32) * mm, "end": v(175.5, 91.25) * mm});
            skLineSegment(sketch, "E322", {"start": v(175.5, -186.25) * mm, "end": v(175.5, 91.25) * mm});
            skArc(sketch, "E323", {"start": v(-167, 16.25) * mm, "mid": v(-164.07, 23.32) * mm, "end": v(-157, 26.25) * mm});
            skArc(sketch, "E324", {"start": v(157, 26.25) * mm, "mid": v(164.07, 23.32) * mm, "end": v(167, 16.25) * mm});
            skArc(sketch, "E325", {"start": v(157, -187.75) * mm, "mid": v(164.07, -184.82) * mm, "end": v(167, -177.75) * mm});
            skArc(sketch, "E326", {"start": v(-157, -187.75) * mm, "mid": v(-164.07, -184.82) * mm, "end": v(-167, -177.75) * mm});
            skLineSegment(sketch, "E327", {"start": v(-157, 26.25) * mm, "end": v(157, 26.25) * mm});
            skCircle(sketch, "E328", {"center": v(-162, -172.75) * mm, "radius": 3 * mm});
            skCircle(sketch, "E329", {"center": v(-162, 11.25) * mm, "radius": 3 * mm});
            skCircle(sketch, "E330", {"center": v(162, 11.25) * mm, "radius": 3 * mm});
            skCircle(sketch, "E331", {"center": v(162, -172.75) * mm, "radius": 3 * mm});
            skLineSegment(sketch, "E332", {"start": v(-167, 16.25) * mm, "end": v(-167, -177.75) * mm});
            skLineSegment(sketch, "E333", {"start": v(167, 16.25) * mm, "end": v(167, -177.75) * mm});
            skCircle(sketch, "E334", {"center": v(-154.5, 23.75) * mm, "radius": 1.5 * mm});
            skCircle(sketch, "E335", {"center": v(154.5, 23.75) * mm, "radius": 1.5 * mm});
            skCircle(sketch, "E336", {"center": v(154.5, -185.25) * mm, "radius": 1.5 * mm});
            skCircle(sketch, "E337", {"center": v(-154.5, -185.25) * mm, "radius": 1.5 * mm});
            skLineSegment(sketch, "E338", {"start": v(-157, -187.75) * mm, "end": v(157, -187.75) * mm});
            skLineSegment(sketch, "E339", {"start": v(-157, -187.75) * mm, "end": v(-157, 26.25) * mm});
            skLineSegment(sketch, "E340", {"start": v(157, 26.25) * mm, "end": v(157, -187.75) * mm});
            skCircle(sketch, "E341", {"center": v(0, 156.25) * mm, "radius": 10 * mm});
            skCircle(sketch, "E342", {"center": v(0, 156.25) * mm, "radius": 50 * mm});
            skCircle(sketch, "E343", {"center": v(-107.5, 156.25) * mm, "radius": 50 * mm});
            skCircle(sketch, "E344", {"center": v(107.5, 156.25) * mm, "radius": 50 * mm});
            skCircle(sketch, "E345", {"center": v(-107.5, 156.25) * mm, "radius": 10 * mm});
            skCircle(sketch, "E346", {"center": v(107.5, 156.25) * mm, "radius": 10 * mm});
            skLineSegment(sketch, "E347", {"start": v(-455.3, -211.25) * mm, "end": v(-499.6, -211.25) * mm});
            skLineSegment(sketch, "E348", {"start": v(-455.3, -208.35) * mm, "end": v(-455.3, -211.25) * mm});
            skLineSegment(sketch, "E349", {"start": v(-455.3, -208.35) * mm, "end": v(-456.8, -208.35) * mm});
            skLineSegment(sketch, "E350", {"start": v(-456.8, -205.75) * mm, "end": v(-456.8, -208.35) * mm});
            skLineSegment(sketch, "E351", {"start": v(-455.3, -205.75) * mm, "end": v(-456.8, -205.75) * mm});
            skLineSegment(sketch, "E352", {"start": v(-455.3, -202.75) * mm, "end": v(-455.3, -205.75) * mm});
            skLineSegment(sketch, "E353", {"start": v(-451.9, -202.75) * mm, "end": v(-455.3, -202.75) * mm});
            skLineSegment(sketch, "E354", {"start": v(-451.9, -205.75) * mm, "end": v(-451.9, -202.75) * mm});
            skLineSegment(sketch, "E355", {"start": v(-450.4, -205.75) * mm, "end": v(-451.9, -205.75) * mm});
            skLineSegment(sketch, "E356", {"start": v(-450.4, -208.35) * mm, "end": v(-450.4, -205.75) * mm});
            skLineSegment(sketch, "E357", {"start": v(-450.4, -208.35) * mm, "end": v(-451.9, -208.35) * mm});
            skLineSegment(sketch, "E358", {"start": v(-451.9, -211.25) * mm, "end": v(-451.9, -208.35) * mm});
            skLineSegment(sketch, "E359", {"start": v(-447.6, -211.25) * mm, "end": v(-451.9, -211.25) * mm});
            skLineSegment(sketch, "E360", {"start": v(-447.6, -214.25) * mm, "end": v(-447.6, -211.25) * mm});
            skLineSegment(sketch, "E361", {"start": v(-437.6, -214.25) * mm, "end": v(-447.6, -214.25) * mm});
            skLineSegment(sketch, "E362", {"start": v(-437.6, -211.25) * mm, "end": v(-437.6, -214.25) * mm});
            skLineSegment(sketch, "E363", {"start": v(-387.6, -211.25) * mm, "end": v(-437.6, -211.25) * mm});
            skLineSegment(sketch, "E364", {"start": v(-387.6, -214.25) * mm, "end": v(-387.6, -211.25) * mm});
            skLineSegment(sketch, "E365", {"start": v(-377.6, -214.25) * mm, "end": v(-387.6, -214.25) * mm});
            skLineSegment(sketch, "E366", {"start": v(-377.6, -211.25) * mm, "end": v(-377.6, -214.25) * mm});
            skLineSegment(sketch, "E367", {"start": v(-354.3, -211.25) * mm, "end": v(-377.6, -211.25) * mm});
            skLineSegment(sketch, "E368", {"start": v(-354.3, -208.35) * mm, "end": v(-354.3, -211.25) * mm});
            skLineSegment(sketch, "E369", {"start": v(-355.8, -208.35) * mm, "end": v(-354.3, -208.35) * mm});
            skLineSegment(sketch, "E370", {"start": v(-355.8, -205.75) * mm, "end": v(-355.8, -208.35) * mm});
            skLineSegment(sketch, "E371", {"start": v(-354.3, -205.75) * mm, "end": v(-355.8, -205.75) * mm});
            skLineSegment(sketch, "E372", {"start": v(-354.3, -202.75) * mm, "end": v(-354.3, -205.75) * mm});
            skLineSegment(sketch, "E373", {"start": v(-350.9, -202.75) * mm, "end": v(-354.3, -202.75) * mm});
            skLineSegment(sketch, "E374", {"start": v(-350.9, -205.75) * mm, "end": v(-350.9, -202.75) * mm});
            skLineSegment(sketch, "E375", {"start": v(-349.4, -205.75) * mm, "end": v(-350.9, -205.75) * mm});
            skLineSegment(sketch, "E376", {"start": v(-349.4, -208.35) * mm, "end": v(-349.4, -205.75) * mm});
            skLineSegment(sketch, "E377", {"start": v(-350.9, -208.35) * mm, "end": v(-349.4, -208.35) * mm});
            skLineSegment(sketch, "E378", {"start": v(-350.9, -211.25) * mm, "end": v(-350.9, -208.35) * mm});
            skLineSegment(sketch, "E379", {"start": v(-327.6, -211.25) * mm, "end": v(-350.9, -211.25) * mm});
            skLineSegment(sketch, "E380", {"start": v(-327.6, -214.25) * mm, "end": v(-327.6, -211.25) * mm});
            skLineSegment(sketch, "E381", {"start": v(-309.1, -214.25) * mm, "end": v(-327.6, -214.25) * mm});
            skLineSegment(sketch, "E382", {"start": v(-309.1, -211.25) * mm, "end": v(-309.1, -214.25) * mm});
            skArc(sketch, "E383", {"start": v(-299.1, -201.25) * mm, "mid": v(-302.03, -208.32) * mm, "end": v(-309.1, -211.25) * mm});
            skLineSegment(sketch, "E384", {"start": v(-296.1, -201.25) * mm, "end": v(-299.1, -201.25) * mm});
            skLineSegment(sketch, "E385", {"start": v(-296.1, -188.25) * mm, "end": v(-296.1, -201.25) * mm});
            skLineSegment(sketch, "E386", {"start": v(-299.1, -188.25) * mm, "end": v(-296.1, -188.25) * mm});
            skLineSegment(sketch, "E387", {"start": v(-299.1, -179.45) * mm, "end": v(-299.1, -188.25) * mm});
            skLineSegment(sketch, "E388", {"start": v(-305.5, -179.45) * mm, "end": v(-299.1, -179.45) * mm});
            skLineSegment(sketch, "E389", {"start": v(-305.5, -180.95) * mm, "end": v(-305.5, -179.45) * mm});
            skLineSegment(sketch, "E390", {"start": v(-308.1, -180.95) * mm, "end": v(-305.5, -180.95) * mm});
            skLineSegment(sketch, "E391", {"start": v(-308.1, -179.45) * mm, "end": v(-308.1, -180.95) * mm});
            skLineSegment(sketch, "E392", {"start": v(-313.1, -179.45) * mm, "end": v(-308.1, -179.45) * mm});
            skLineSegment(sketch, "E393", {"start": v(-313.1, -176.05) * mm, "end": v(-313.1, -179.45) * mm});
            skLineSegment(sketch, "E394", {"start": v(-308.1, -176.05) * mm, "end": v(-313.1, -176.05) * mm});
            skLineSegment(sketch, "E395", {"start": v(-308.1, -174.55) * mm, "end": v(-308.1, -176.05) * mm});
            skLineSegment(sketch, "E396", {"start": v(-305.5, -174.55) * mm, "end": v(-308.1, -174.55) * mm});
            skLineSegment(sketch, "E397", {"start": v(-305.5, -176.05) * mm, "end": v(-305.5, -174.55) * mm});
            skLineSegment(sketch, "E398", {"start": v(-299.1, -176.05) * mm, "end": v(-305.5, -176.05) * mm});
            skLineSegment(sketch, "E399", {"start": v(-299.1, -138.25) * mm, "end": v(-299.1, -176.05) * mm});
            skLineSegment(sketch, "E400", {"start": v(-296.1, -138.25) * mm, "end": v(-299.1, -138.25) * mm});
            skLineSegment(sketch, "E401", {"start": v(-296.1, -128.25) * mm, "end": v(-296.1, -138.25) * mm});
            skLineSegment(sketch, "E402", {"start": v(-299.1, -128.25) * mm, "end": v(-296.1, -128.25) * mm});
            skLineSegment(sketch, "E403", {"start": v(-299.1, -78.25) * mm, "end": v(-299.1, -128.25) * mm});
            skLineSegment(sketch, "E404", {"start": v(-296.1, -78.25) * mm, "end": v(-299.1, -78.25) * mm});
            skLineSegment(sketch, "E405", {"start": v(-296.1, -68.25) * mm, "end": v(-296.1, -78.25) * mm});
            skLineSegment(sketch, "E406", {"start": v(-299.1, -68.25) * mm, "end": v(-296.1, -68.25) * mm});
            skLineSegment(sketch, "E407", {"start": v(-299.1, -58.45) * mm, "end": v(-299.1, -68.25) * mm});
            skLineSegment(sketch, "E408", {"start": v(-305.5, -58.45) * mm, "end": v(-299.1, -58.45) * mm});
            skLineSegment(sketch, "E409", {"start": v(-305.5, -59.95) * mm, "end": v(-305.5, -58.45) * mm});
            skLineSegment(sketch, "E410", {"start": v(-308.1, -59.95) * mm, "end": v(-305.5, -59.95) * mm});
            skLineSegment(sketch, "E411", {"start": v(-308.1, -58.45) * mm, "end": v(-308.1, -59.95) * mm});
            skLineSegment(sketch, "E412", {"start": v(-313.1, -58.45) * mm, "end": v(-308.1, -58.45) * mm});
            skLineSegment(sketch, "E413", {"start": v(-313.1, -55.05) * mm, "end": v(-313.1, -58.45) * mm});
            skLineSegment(sketch, "E414", {"start": v(-308.1, -55.05) * mm, "end": v(-313.1, -55.05) * mm});
            skLineSegment(sketch, "E415", {"start": v(-308.1, -53.55) * mm, "end": v(-308.1, -55.05) * mm});
            skLineSegment(sketch, "E416", {"start": v(-305.5, -53.55) * mm, "end": v(-308.1, -53.55) * mm});
            skLineSegment(sketch, "E417", {"start": v(-305.5, -55.05) * mm, "end": v(-305.5, -53.55) * mm});
            skLineSegment(sketch, "E418", {"start": v(-299.1, -55.05) * mm, "end": v(-305.5, -55.05) * mm});
            skLineSegment(sketch, "E419", {"start": v(-299.1, -16.25) * mm, "end": v(-299.1, -55.05) * mm});
            skLineSegment(sketch, "E420", {"start": v(-296.1, -16.25) * mm, "end": v(-299.1, -16.25) * mm});
            skLineSegment(sketch, "E421", {"start": v(-296.1, -6.25) * mm, "end": v(-296.1, -16.25) * mm});
            skLineSegment(sketch, "E422", {"start": v(-299.1, -6.25) * mm, "end": v(-296.1, -6.25) * mm});
            skLineSegment(sketch, "E423", {"start": v(-299.1, 33.55) * mm, "end": v(-299.1, -6.25) * mm});
            skLineSegment(sketch, "E424", {"start": v(-305.5, 33.55) * mm, "end": v(-299.1, 33.55) * mm});
            skLineSegment(sketch, "E425", {"start": v(-305.5, 33.55) * mm, "end": v(-305.5, 32.05) * mm});
            skLineSegment(sketch, "E426", {"start": v(-308.1, 32.05) * mm, "end": v(-305.5, 32.05) * mm});
            skLineSegment(sketch, "E427", {"start": v(-308.1, 33.55) * mm, "end": v(-308.1, 32.05) * mm});
            skLineSegment(sketch, "E428", {"start": v(-313.1, 33.55) * mm, "end": v(-308.1, 33.55) * mm});
            skLineSegment(sketch, "E429", {"start": v(-313.1, 36.95) * mm, "end": v(-313.1, 33.55) * mm});
            skLineSegment(sketch, "E430", {"start": v(-308.1, 36.95) * mm, "end": v(-313.1, 36.95) * mm});
            skLineSegment(sketch, "E431", {"start": v(-308.1, 38.45) * mm, "end": v(-308.1, 36.95) * mm});
            skLineSegment(sketch, "E432", {"start": v(-305.5, 38.45) * mm, "end": v(-308.1, 38.45) * mm});
            skLineSegment(sketch, "E433", {"start": v(-305.5, 38.45) * mm, "end": v(-305.5, 36.95) * mm});
            skLineSegment(sketch, "E434", {"start": v(-299.1, 36.95) * mm, "end": v(-305.5, 36.95) * mm});
            skLineSegment(sketch, "E435", {"start": v(-299.1, 45.75) * mm, "end": v(-299.1, 36.95) * mm});
            skLineSegment(sketch, "E436", {"start": v(-296.1, 45.75) * mm, "end": v(-299.1, 45.75) * mm});
            skLineSegment(sketch, "E437", {"start": v(-296.1, 55.75) * mm, "end": v(-296.1, 45.75) * mm});
            skLineSegment(sketch, "E438", {"start": v(-299.1, 55.75) * mm, "end": v(-296.1, 55.75) * mm});
            skLineSegment(sketch, "E439", {"start": v(-299.1, 105.75) * mm, "end": v(-299.1, 55.75) * mm});
            skLineSegment(sketch, "E440", {"start": v(-296.1, 105.75) * mm, "end": v(-299.1, 105.75) * mm});
            skLineSegment(sketch, "E441", {"start": v(-296.1, 115.75) * mm, "end": v(-296.1, 105.75) * mm});
            skLineSegment(sketch, "E442", {"start": v(-299.1, 115.75) * mm, "end": v(-296.1, 115.75) * mm});
            skLineSegment(sketch, "E443", {"start": v(-299.1, 124.55) * mm, "end": v(-299.1, 115.75) * mm});
            skLineSegment(sketch, "E444", {"start": v(-305.5, 124.55) * mm, "end": v(-299.1, 124.55) * mm});
            skLineSegment(sketch, "E445", {"start": v(-305.5, 123.05) * mm, "end": v(-305.5, 124.55) * mm});
            skLineSegment(sketch, "E446", {"start": v(-308.1, 123.05) * mm, "end": v(-305.5, 123.05) * mm});
            skLineSegment(sketch, "E447", {"start": v(-308.1, 124.55) * mm, "end": v(-308.1, 123.05) * mm});
            skLineSegment(sketch, "E448", {"start": v(-313.1, 124.55) * mm, "end": v(-308.1, 124.55) * mm});
            skLineSegment(sketch, "E449", {"start": v(-313.1, 127.95) * mm, "end": v(-313.1, 124.55) * mm});
            skLineSegment(sketch, "E450", {"start": v(-308.1, 127.95) * mm, "end": v(-313.1, 127.95) * mm});
            skLineSegment(sketch, "E451", {"start": v(-308.1, 129.45) * mm, "end": v(-308.1, 127.95) * mm});
            skLineSegment(sketch, "E452", {"start": v(-305.5, 129.45) * mm, "end": v(-308.1, 129.45) * mm});
            skLineSegment(sketch, "E453", {"start": v(-305.5, 127.95) * mm, "end": v(-305.5, 129.45) * mm});
            skLineSegment(sketch, "E454", {"start": v(-299.1, 127.95) * mm, "end": v(-305.5, 127.95) * mm});
            skLineSegment(sketch, "E455", {"start": v(-299.1, 181.25) * mm, "end": v(-299.1, 127.95) * mm});
            skLineSegment(sketch, "E456", {"start": v(-296.1, 181.25) * mm, "end": v(-299.1, 181.25) * mm});
            skLineSegment(sketch, "E457", {"start": v(-296.1, 201.25) * mm, "end": v(-296.1, 181.25) * mm});
            skLineSegment(sketch, "E458", {"start": v(-299.1, 201.25) * mm, "end": v(-296.1, 201.25) * mm});
            skArc(sketch, "E459", {"start": v(-309.1, 211.25) * mm, "mid": v(-302.03, 208.32) * mm, "end": v(-299.1, 201.25) * mm});
            skLineSegment(sketch, "E460", {"start": v(-309.1, 214.25) * mm, "end": v(-309.1, 211.25) * mm});
            skLineSegment(sketch, "E461", {"start": v(-327.6, 214.25) * mm, "end": v(-309.1, 214.25) * mm});
            skLineSegment(sketch, "E462", {"start": v(-327.6, 211.25) * mm, "end": v(-327.6, 214.25) * mm});
            skLineSegment(sketch, "E463", {"start": v(-350.9, 211.25) * mm, "end": v(-327.6, 211.25) * mm});
            skLineSegment(sketch, "E464", {"start": v(-350.9, 204.85) * mm, "end": v(-350.9, 211.25) * mm});
            skLineSegment(sketch, "E465", {"start": v(-349.4, 204.85) * mm, "end": v(-350.9, 204.85) * mm});
            skLineSegment(sketch, "E466", {"start": v(-349.4, 202.25) * mm, "end": v(-349.4, 204.85) * mm});
            skLineSegment(sketch, "E467", {"start": v(-350.9, 202.25) * mm, "end": v(-349.4, 202.25) * mm});
            skLineSegment(sketch, "E468", {"start": v(-350.9, 197.25) * mm, "end": v(-350.9, 202.25) * mm});
            skLineSegment(sketch, "E469", {"start": v(-354.3, 197.25) * mm, "end": v(-350.9, 197.25) * mm});
            skLineSegment(sketch, "E470", {"start": v(-354.3, 202.25) * mm, "end": v(-354.3, 197.25) * mm});
            skLineSegment(sketch, "E471", {"start": v(-355.8, 202.25) * mm, "end": v(-354.3, 202.25) * mm});
            skLineSegment(sketch, "E472", {"start": v(-355.8, 204.85) * mm, "end": v(-355.8, 202.25) * mm});
            skLineSegment(sketch, "E473", {"start": v(-354.3, 204.85) * mm, "end": v(-355.8, 204.85) * mm});
            skLineSegment(sketch, "E474", {"start": v(-354.3, 211.25) * mm, "end": v(-354.3, 204.85) * mm});
            skLineSegment(sketch, "E475", {"start": v(-377.6, 211.25) * mm, "end": v(-354.3, 211.25) * mm});
            skLineSegment(sketch, "E476", {"start": v(-377.6, 214.25) * mm, "end": v(-377.6, 211.25) * mm});
            skLineSegment(sketch, "E477", {"start": v(-387.6, 214.25) * mm, "end": v(-377.6, 214.25) * mm});
            skLineSegment(sketch, "E478", {"start": v(-387.6, 211.25) * mm, "end": v(-387.6, 214.25) * mm});
            skLineSegment(sketch, "E479", {"start": v(-437.6, 211.25) * mm, "end": v(-387.6, 211.25) * mm});
            skLineSegment(sketch, "E480", {"start": v(-437.6, 214.25) * mm, "end": v(-437.6, 211.25) * mm});
            skLineSegment(sketch, "E481", {"start": v(-447.6, 214.25) * mm, "end": v(-437.6, 214.25) * mm});
            skLineSegment(sketch, "E482", {"start": v(-447.6, 211.25) * mm, "end": v(-447.6, 214.25) * mm});
            skLineSegment(sketch, "E483", {"start": v(-451.9, 211.25) * mm, "end": v(-447.6, 211.25) * mm});
            skLineSegment(sketch, "E484", {"start": v(-451.9, 204.85) * mm, "end": v(-451.9, 211.25) * mm});
            skLineSegment(sketch, "E485", {"start": v(-450.4, 204.85) * mm, "end": v(-451.9, 204.85) * mm});
            skLineSegment(sketch, "E486", {"start": v(-450.4, 202.25) * mm, "end": v(-450.4, 204.85) * mm});
            skLineSegment(sketch, "E487", {"start": v(-450.4, 202.25) * mm, "end": v(-451.9, 202.25) * mm});
            skLineSegment(sketch, "E488", {"start": v(-451.9, 197.25) * mm, "end": v(-451.9, 202.25) * mm});
            skLineSegment(sketch, "E489", {"start": v(-455.3, 197.25) * mm, "end": v(-451.9, 197.25) * mm});
            skLineSegment(sketch, "E490", {"start": v(-455.3, 202.25) * mm, "end": v(-455.3, 197.25) * mm});
            skLineSegment(sketch, "E491", {"start": v(-455.3, 202.25) * mm, "end": v(-456.8, 202.25) * mm});
            skLineSegment(sketch, "E492", {"start": v(-456.8, 204.85) * mm, "end": v(-456.8, 202.25) * mm});
            skLineSegment(sketch, "E493", {"start": v(-455.3, 204.85) * mm, "end": v(-456.8, 204.85) * mm});
            skLineSegment(sketch, "E494", {"start": v(-455.3, 211.25) * mm, "end": v(-455.3, 204.85) * mm});
            skLineSegment(sketch, "E495", {"start": v(-499.6, 211.25) * mm, "end": v(-455.3, 211.25) * mm});
            skLineSegment(sketch, "E496", {"start": v(-499.6, 214.25) * mm, "end": v(-499.6, 211.25) * mm});
            skLineSegment(sketch, "E497", {"start": v(-509.6, 214.25) * mm, "end": v(-499.6, 214.25) * mm});
            skLineSegment(sketch, "E498", {"start": v(-509.6, 211.25) * mm, "end": v(-509.6, 214.25) * mm});
            skLineSegment(sketch, "E499", {"start": v(-553.9, 211.25) * mm, "end": v(-509.6, 211.25) * mm});
            skLineSegment(sketch, "E500", {"start": v(-553.9, 204.85) * mm, "end": v(-553.9, 211.25) * mm});
            skLineSegment(sketch, "E501", {"start": v(-553.9, 204.85) * mm, "end": v(-552.4, 204.85) * mm});
            skLineSegment(sketch, "E502", {"start": v(-552.4, 202.25) * mm, "end": v(-552.4, 204.85) * mm});
            skLineSegment(sketch, "E503", {"start": v(-553.9, 202.25) * mm, "end": v(-552.4, 202.25) * mm});
            skLineSegment(sketch, "E504", {"start": v(-553.9, 197.25) * mm, "end": v(-553.9, 202.25) * mm});
            skLineSegment(sketch, "E505", {"start": v(-557.3, 197.25) * mm, "end": v(-553.9, 197.25) * mm});
            skLineSegment(sketch, "E506", {"start": v(-557.3, 202.25) * mm, "end": v(-557.3, 197.25) * mm});
            skLineSegment(sketch, "E507", {"start": v(-558.8, 202.25) * mm, "end": v(-557.3, 202.25) * mm});
            skLineSegment(sketch, "E508", {"start": v(-558.8, 204.85) * mm, "end": v(-558.8, 202.25) * mm});
            skLineSegment(sketch, "E509", {"start": v(-558.8, 204.85) * mm, "end": v(-557.3, 204.85) * mm});
            skLineSegment(sketch, "E510", {"start": v(-557.3, 211.25) * mm, "end": v(-557.3, 204.85) * mm});
            skLineSegment(sketch, "E511", {"start": v(-561.6, 211.25) * mm, "end": v(-557.3, 211.25) * mm});
            skLineSegment(sketch, "E512", {"start": v(-561.6, 214.25) * mm, "end": v(-561.6, 211.25) * mm});
            skLineSegment(sketch, "E513", {"start": v(-571.6, 214.25) * mm, "end": v(-561.6, 214.25) * mm});
            skLineSegment(sketch, "E514", {"start": v(-571.6, 211.25) * mm, "end": v(-571.6, 214.25) * mm});
            skLineSegment(sketch, "E515", {"start": v(-621.6, 211.25) * mm, "end": v(-571.6, 211.25) * mm});
            skLineSegment(sketch, "E516", {"start": v(-621.6, 214.25) * mm, "end": v(-621.6, 211.25) * mm});
            skLineSegment(sketch, "E517", {"start": v(-631.6, 214.25) * mm, "end": v(-621.6, 214.25) * mm});
            skLineSegment(sketch, "E518", {"start": v(-631.6, 211.25) * mm, "end": v(-631.6, 214.25) * mm});
            skLineSegment(sketch, "E519", {"start": v(-654.9, 211.25) * mm, "end": v(-631.6, 211.25) * mm});
            skLineSegment(sketch, "E520", {"start": v(-654.9, 204.85) * mm, "end": v(-654.9, 211.25) * mm});
            skLineSegment(sketch, "E521", {"start": v(-653.4, 204.85) * mm, "end": v(-654.9, 204.85) * mm});
            skLineSegment(sketch, "E522", {"start": v(-653.4, 202.25) * mm, "end": v(-653.4, 204.85) * mm});
            skLineSegment(sketch, "E523", {"start": v(-654.9, 202.25) * mm, "end": v(-653.4, 202.25) * mm});
            skLineSegment(sketch, "E524", {"start": v(-654.9, 197.25) * mm, "end": v(-654.9, 202.25) * mm});
            skLineSegment(sketch, "E525", {"start": v(-658.3, 197.25) * mm, "end": v(-654.9, 197.25) * mm});
            skLineSegment(sketch, "E526", {"start": v(-658.3, 202.25) * mm, "end": v(-658.3, 197.25) * mm});
            skLineSegment(sketch, "E527", {"start": v(-659.8, 202.25) * mm, "end": v(-658.3, 202.25) * mm});
            skLineSegment(sketch, "E528", {"start": v(-659.8, 204.85) * mm, "end": v(-659.8, 202.25) * mm});
            skLineSegment(sketch, "E529", {"start": v(-658.3, 204.85) * mm, "end": v(-659.8, 204.85) * mm});
            skLineSegment(sketch, "E530", {"start": v(-658.3, 211.25) * mm, "end": v(-658.3, 204.85) * mm});
            skLineSegment(sketch, "E531", {"start": v(-681.6, 211.25) * mm, "end": v(-658.3, 211.25) * mm});
            skLineSegment(sketch, "E532", {"start": v(-681.6, 214.25) * mm, "end": v(-681.6, 211.25) * mm});
            skLineSegment(sketch, "E533", {"start": v(-700.1, 214.25) * mm, "end": v(-681.6, 214.25) * mm});
            skLineSegment(sketch, "E534", {"start": v(-700.1, 211.25) * mm, "end": v(-700.1, 214.25) * mm});
            skArc(sketch, "E535", {"start": v(-710.1, 201.25) * mm, "mid": v(-707.17, 208.32) * mm, "end": v(-700.1, 211.25) * mm});
            skLineSegment(sketch, "E536", {"start": v(-713.1, 201.25) * mm, "end": v(-710.1, 201.25) * mm});
            skLineSegment(sketch, "E537", {"start": v(-713.1, 181.25) * mm, "end": v(-713.1, 201.25) * mm});
            skLineSegment(sketch, "E538", {"start": v(-710.1, 181.25) * mm, "end": v(-713.1, 181.25) * mm});
            skLineSegment(sketch, "E539", {"start": v(-710.1, 127.95) * mm, "end": v(-710.1, 181.25) * mm});
            skLineSegment(sketch, "E540", {"start": v(-703.7, 127.95) * mm, "end": v(-710.1, 127.95) * mm});
            skLineSegment(sketch, "E541", {"start": v(-703.7, 129.45) * mm, "end": v(-703.7, 127.95) * mm});
            skLineSegment(sketch, "E542", {"start": v(-701.1, 129.45) * mm, "end": v(-703.7, 129.45) * mm});
            skLineSegment(sketch, "E543", {"start": v(-701.1, 127.95) * mm, "end": v(-701.1, 129.45) * mm});
            skLineSegment(sketch, "E544", {"start": v(-696.1, 127.95) * mm, "end": v(-701.1, 127.95) * mm});
            skLineSegment(sketch, "E545", {"start": v(-696.1, 124.55) * mm, "end": v(-696.1, 127.95) * mm});
            skLineSegment(sketch, "E546", {"start": v(-701.1, 124.55) * mm, "end": v(-696.1, 124.55) * mm});
            skLineSegment(sketch, "E547", {"start": v(-701.1, 123.05) * mm, "end": v(-701.1, 124.55) * mm});
            skLineSegment(sketch, "E548", {"start": v(-703.7, 123.05) * mm, "end": v(-701.1, 123.05) * mm});
            skLineSegment(sketch, "E549", {"start": v(-703.7, 124.55) * mm, "end": v(-703.7, 123.05) * mm});
            skLineSegment(sketch, "E550", {"start": v(-710.1, 124.55) * mm, "end": v(-703.7, 124.55) * mm});
            skLineSegment(sketch, "E551", {"start": v(-710.1, 115.75) * mm, "end": v(-710.1, 124.55) * mm});
            skLineSegment(sketch, "E552", {"start": v(-713.1, 115.75) * mm, "end": v(-710.1, 115.75) * mm});
            skLineSegment(sketch, "E553", {"start": v(-713.1, 105.75) * mm, "end": v(-713.1, 115.75) * mm});
            skLineSegment(sketch, "E554", {"start": v(-710.1, 105.75) * mm, "end": v(-713.1, 105.75) * mm});
            skLineSegment(sketch, "E555", {"start": v(-710.1, 55.75) * mm, "end": v(-710.1, 105.75) * mm});
            skLineSegment(sketch, "E556", {"start": v(-713.1, 55.75) * mm, "end": v(-710.1, 55.75) * mm});
            skLineSegment(sketch, "E557", {"start": v(-713.1, 45.75) * mm, "end": v(-713.1, 55.75) * mm});
            skLineSegment(sketch, "E558", {"start": v(-710.1, 45.75) * mm, "end": v(-713.1, 45.75) * mm});
            skLineSegment(sketch, "E559", {"start": v(-710.1, 36.95) * mm, "end": v(-710.1, 45.75) * mm});
            skLineSegment(sketch, "E560", {"start": v(-703.7, 36.95) * mm, "end": v(-710.1, 36.95) * mm});
            skLineSegment(sketch, "E561", {"start": v(-703.7, 38.45) * mm, "end": v(-703.7, 36.95) * mm});
            skLineSegment(sketch, "E562", {"start": v(-701.1, 38.45) * mm, "end": v(-703.7, 38.45) * mm});
            skLineSegment(sketch, "E563", {"start": v(-701.1, 38.45) * mm, "end": v(-701.1, 36.95) * mm});
            skLineSegment(sketch, "E564", {"start": v(-696.1, 36.95) * mm, "end": v(-701.1, 36.95) * mm});
            skLineSegment(sketch, "E565", {"start": v(-696.1, 33.55) * mm, "end": v(-696.1, 36.95) * mm});
            skLineSegment(sketch, "E566", {"start": v(-701.1, 33.55) * mm, "end": v(-696.1, 33.55) * mm});
            skLineSegment(sketch, "E567", {"start": v(-701.1, 33.55) * mm, "end": v(-701.1, 32.05) * mm});
            skLineSegment(sketch, "E568", {"start": v(-703.7, 32.05) * mm, "end": v(-701.1, 32.05) * mm});
            skLineSegment(sketch, "E569", {"start": v(-703.7, 33.55) * mm, "end": v(-703.7, 32.05) * mm});
            skLineSegment(sketch, "E570", {"start": v(-710.1, 33.55) * mm, "end": v(-703.7, 33.55) * mm});
            skLineSegment(sketch, "E571", {"start": v(-710.1, -6.25) * mm, "end": v(-710.1, 33.55) * mm});
            skLineSegment(sketch, "E572", {"start": v(-713.1, -6.25) * mm, "end": v(-710.1, -6.25) * mm});
            skLineSegment(sketch, "E573", {"start": v(-713.1, -16.25) * mm, "end": v(-713.1, -6.25) * mm});
            skLineSegment(sketch, "E574", {"start": v(-710.1, -16.25) * mm, "end": v(-713.1, -16.25) * mm});
            skLineSegment(sketch, "E575", {"start": v(-710.1, -55.05) * mm, "end": v(-710.1, -16.25) * mm});
            skLineSegment(sketch, "E576", {"start": v(-703.7, -55.05) * mm, "end": v(-710.1, -55.05) * mm});
            skLineSegment(sketch, "E577", {"start": v(-703.7, -53.55) * mm, "end": v(-703.7, -55.05) * mm});
            skLineSegment(sketch, "E578", {"start": v(-701.1, -53.55) * mm, "end": v(-703.7, -53.55) * mm});
            skLineSegment(sketch, "E579", {"start": v(-701.1, -55.05) * mm, "end": v(-701.1, -53.55) * mm});
            skLineSegment(sketch, "E580", {"start": v(-696.1, -55.05) * mm, "end": v(-701.1, -55.05) * mm});
            skLineSegment(sketch, "E581", {"start": v(-696.1, -58.45) * mm, "end": v(-696.1, -55.05) * mm});
            skLineSegment(sketch, "E582", {"start": v(-701.1, -58.45) * mm, "end": v(-696.1, -58.45) * mm});
            skLineSegment(sketch, "E583", {"start": v(-701.1, -59.95) * mm, "end": v(-701.1, -58.45) * mm});
            skLineSegment(sketch, "E584", {"start": v(-703.7, -59.95) * mm, "end": v(-701.1, -59.95) * mm});
            skLineSegment(sketch, "E585", {"start": v(-703.7, -58.45) * mm, "end": v(-703.7, -59.95) * mm});
            skLineSegment(sketch, "E586", {"start": v(-710.1, -58.45) * mm, "end": v(-703.7, -58.45) * mm});
            skLineSegment(sketch, "E587", {"start": v(-710.1, -68.25) * mm, "end": v(-710.1, -58.45) * mm});
            skLineSegment(sketch, "E588", {"start": v(-713.1, -68.25) * mm, "end": v(-710.1, -68.25) * mm});
            skLineSegment(sketch, "E589", {"start": v(-713.1, -78.25) * mm, "end": v(-713.1, -68.25) * mm});
            skLineSegment(sketch, "E590", {"start": v(-710.1, -78.25) * mm, "end": v(-713.1, -78.25) * mm});
            skLineSegment(sketch, "E591", {"start": v(-710.1, -128.25) * mm, "end": v(-710.1, -78.25) * mm});
            skLineSegment(sketch, "E592", {"start": v(-713.1, -128.25) * mm, "end": v(-710.1, -128.25) * mm});
            skLineSegment(sketch, "E593", {"start": v(-713.1, -138.25) * mm, "end": v(-713.1, -128.25) * mm});
            skLineSegment(sketch, "E594", {"start": v(-710.1, -138.25) * mm, "end": v(-713.1, -138.25) * mm});
            skLineSegment(sketch, "E595", {"start": v(-710.1, -176.05) * mm, "end": v(-710.1, -138.25) * mm});
            skLineSegment(sketch, "E596", {"start": v(-703.7, -176.05) * mm, "end": v(-710.1, -176.05) * mm});
            skLineSegment(sketch, "E597", {"start": v(-703.7, -174.55) * mm, "end": v(-703.7, -176.05) * mm});
            skLineSegment(sketch, "E598", {"start": v(-701.1, -174.55) * mm, "end": v(-703.7, -174.55) * mm});
            skLineSegment(sketch, "E599", {"start": v(-701.1, -176.05) * mm, "end": v(-701.1, -174.55) * mm});
            skLineSegment(sketch, "E600", {"start": v(-696.1, -176.05) * mm, "end": v(-701.1, -176.05) * mm});
            skLineSegment(sketch, "E601", {"start": v(-696.1, -179.45) * mm, "end": v(-696.1, -176.05) * mm});
            skLineSegment(sketch, "E602", {"start": v(-701.1, -179.45) * mm, "end": v(-696.1, -179.45) * mm});
            skLineSegment(sketch, "E603", {"start": v(-701.1, -180.95) * mm, "end": v(-701.1, -179.45) * mm});
            skLineSegment(sketch, "E604", {"start": v(-703.7, -180.95) * mm, "end": v(-701.1, -180.95) * mm});
            skLineSegment(sketch, "E605", {"start": v(-703.7, -179.45) * mm, "end": v(-703.7, -180.95) * mm});
            skLineSegment(sketch, "E606", {"start": v(-710.1, -179.45) * mm, "end": v(-703.7, -179.45) * mm});
            skLineSegment(sketch, "E607", {"start": v(-710.1, -188.25) * mm, "end": v(-710.1, -179.45) * mm});
            skLineSegment(sketch, "E608", {"start": v(-713.1, -188.25) * mm, "end": v(-710.1, -188.25) * mm});
            skLineSegment(sketch, "E609", {"start": v(-713.1, -201.25) * mm, "end": v(-713.1, -188.25) * mm});
            skLineSegment(sketch, "E610", {"start": v(-710.1, -201.25) * mm, "end": v(-713.1, -201.25) * mm});
            skArc(sketch, "E611", {"start": v(-710.1, -201.25) * mm, "mid": v(-707.17, -208.32) * mm, "end": v(-700.1, -211.25) * mm});
            skLineSegment(sketch, "E612", {"start": v(-700.1, -214.25) * mm, "end": v(-700.1, -211.25) * mm});
            skLineSegment(sketch, "E613", {"start": v(-681.6, -214.25) * mm, "end": v(-700.1, -214.25) * mm});
            skLineSegment(sketch, "E614", {"start": v(-681.6, -211.25) * mm, "end": v(-681.6, -214.25) * mm});
            skLineSegment(sketch, "E615", {"start": v(-658.3, -211.25) * mm, "end": v(-681.6, -211.25) * mm});
            skLineSegment(sketch, "E616", {"start": v(-658.3, -208.35) * mm, "end": v(-658.3, -211.25) * mm});
            skLineSegment(sketch, "E617", {"start": v(-659.8, -208.35) * mm, "end": v(-658.3, -208.35) * mm});
            skLineSegment(sketch, "E618", {"start": v(-659.8, -205.75) * mm, "end": v(-659.8, -208.35) * mm});
            skLineSegment(sketch, "E619", {"start": v(-658.3, -205.75) * mm, "end": v(-659.8, -205.75) * mm});
            skLineSegment(sketch, "E620", {"start": v(-658.3, -202.75) * mm, "end": v(-658.3, -205.75) * mm});
            skLineSegment(sketch, "E621", {"start": v(-654.9, -202.75) * mm, "end": v(-658.3, -202.75) * mm});
            skLineSegment(sketch, "E622", {"start": v(-654.9, -205.75) * mm, "end": v(-654.9, -202.75) * mm});
            skLineSegment(sketch, "E623", {"start": v(-653.4, -205.75) * mm, "end": v(-654.9, -205.75) * mm});
            skLineSegment(sketch, "E624", {"start": v(-653.4, -208.35) * mm, "end": v(-653.4, -205.75) * mm});
            skLineSegment(sketch, "E625", {"start": v(-654.9, -208.35) * mm, "end": v(-653.4, -208.35) * mm});
            skLineSegment(sketch, "E626", {"start": v(-654.9, -211.25) * mm, "end": v(-654.9, -208.35) * mm});
            skLineSegment(sketch, "E627", {"start": v(-631.6, -211.25) * mm, "end": v(-654.9, -211.25) * mm});
            skLineSegment(sketch, "E628", {"start": v(-631.6, -214.25) * mm, "end": v(-631.6, -211.25) * mm});
            skLineSegment(sketch, "E629", {"start": v(-621.6, -214.25) * mm, "end": v(-631.6, -214.25) * mm});
            skLineSegment(sketch, "E630", {"start": v(-621.6, -211.25) * mm, "end": v(-621.6, -214.25) * mm});
            skLineSegment(sketch, "E631", {"start": v(-571.6, -211.25) * mm, "end": v(-621.6, -211.25) * mm});
            skLineSegment(sketch, "E632", {"start": v(-571.6, -214.25) * mm, "end": v(-571.6, -211.25) * mm});
            skLineSegment(sketch, "E633", {"start": v(-561.6, -214.25) * mm, "end": v(-571.6, -214.25) * mm});
            skLineSegment(sketch, "E634", {"start": v(-561.6, -211.25) * mm, "end": v(-561.6, -214.25) * mm});
            skLineSegment(sketch, "E635", {"start": v(-557.3, -211.25) * mm, "end": v(-561.6, -211.25) * mm});
            skLineSegment(sketch, "E636", {"start": v(-557.3, -208.35) * mm, "end": v(-557.3, -211.25) * mm});
            skLineSegment(sketch, "E637", {"start": v(-558.8, -208.35) * mm, "end": v(-557.3, -208.35) * mm});
            skLineSegment(sketch, "E638", {"start": v(-558.8, -205.75) * mm, "end": v(-558.8, -208.35) * mm});
            skLineSegment(sketch, "E639", {"start": v(-558.8, -205.75) * mm, "end": v(-557.3, -205.75) * mm});
            skLineSegment(sketch, "E640", {"start": v(-557.3, -202.75) * mm, "end": v(-557.3, -205.75) * mm});
            skLineSegment(sketch, "E641", {"start": v(-553.9, -202.75) * mm, "end": v(-557.3, -202.75) * mm});
            skLineSegment(sketch, "E642", {"start": v(-553.9, -205.75) * mm, "end": v(-553.9, -202.75) * mm});
            skLineSegment(sketch, "E643", {"start": v(-553.9, -205.75) * mm, "end": v(-552.4, -205.75) * mm});
            skLineSegment(sketch, "E644", {"start": v(-552.4, -208.35) * mm, "end": v(-552.4, -205.75) * mm});
            skLineSegment(sketch, "E645", {"start": v(-553.9, -208.35) * mm, "end": v(-552.4, -208.35) * mm});
            skLineSegment(sketch, "E646", {"start": v(-553.9, -211.25) * mm, "end": v(-553.9, -208.35) * mm});
            skLineSegment(sketch, "E647", {"start": v(-509.6, -211.25) * mm, "end": v(-553.9, -211.25) * mm});
            skLineSegment(sketch, "E648", {"start": v(-509.6, -214.25) * mm, "end": v(-509.6, -211.25) * mm});
            skLineSegment(sketch, "E649", {"start": v(-499.6, -214.25) * mm, "end": v(-509.6, -214.25) * mm});
            skLineSegment(sketch, "E650", {"start": v(-499.6, -211.25) * mm, "end": v(-499.6, -214.25) * mm});
            skCircle(sketch, "E651", {"center": v(-666.6, -172.75) * mm, "radius": 3 * mm});
            skCircle(sketch, "E652", {"center": v(-666.6, 11.25) * mm, "radius": 3 * mm});
            skCircle(sketch, "E653", {"center": v(-342.6, 11.25) * mm, "radius": 3 * mm});
            skCircle(sketch, "E654", {"center": v(-342.6, -172.75) * mm, "radius": 3 * mm});
            skCircle(sketch, "E655", {"center": v(-504.6, 156.25) * mm, "radius": 10 * mm});
            skCircle(sketch, "E656", {"center": v(-504.6, 156.25) * mm, "radius": 50 * mm});
            skCircle(sketch, "E657", {"center": v(-612.1, 156.25) * mm, "radius": 50 * mm});
            skCircle(sketch, "E658", {"center": v(-397.1, 156.25) * mm, "radius": 50 * mm});
            skCircle(sketch, "E659", {"center": v(-612.1, 156.25) * mm, "radius": 10 * mm});
            skCircle(sketch, "E660", {"center": v(-397.1, 156.25) * mm, "radius": 10 * mm});
            skLineSegment(sketch, "E661.bottom", {"start": v(-1035.67, 33.51) * mm, "end": v(-929.66, 78.1) * mm});
            skLineSegment(sketch, "E661.top", {"start": v(-952.32, -164.68) * mm, "end": v(-846.32, -120.1) * mm});
            skLineSegment(sketch, "E661.left", {"start": v(-1035.67, 33.51) * mm, "end": v(-952.32, -164.68) * mm});
            skLineSegment(sketch, "E661.right", {"start": v(-929.66, 78.1) * mm, "end": v(-846.32, -120.1) * mm});
            skCircle(sketch, "E662", {"center": v(-1110.38, -101.96) * mm, "radius": 105 * mm});
            skLineSegment(sketch, "E663.bottom", {"start": v(-996.7, 215.7) * mm, "end": v(-927.56, 244.77) * mm});
            skLineSegment(sketch, "E663.top", {"start": v(-944.38, 91.25) * mm, "end": v(-875.24, 120.32) * mm});
            skLineSegment(sketch, "E663.left", {"start": v(-996.7, 215.7) * mm, "end": v(-944.38, 91.25) * mm});
            skLineSegment(sketch, "E663.right", {"start": v(-927.56, 244.77) * mm, "end": v(-875.24, 120.32) * mm});
            skLineSegment(sketch, "E664.bottom", {"start": v(-1095.32, 64.96) * mm, "end": v(-1038.92, 64.96) * mm});
            skLineSegment(sketch, "E664.top", {"start": v(-1095.32, 8.56) * mm, "end": v(-1038.92, 8.56) * mm});
            skLineSegment(sketch, "E664.left", {"start": v(-1095.32, 64.96) * mm, "end": v(-1095.32, 8.56) * mm});
            skLineSegment(sketch, "E664.right", {"start": v(-1038.92, 64.96) * mm, "end": v(-1038.92, 8.56) * mm});
            skCircle(sketch, "E665", {"center": v(-1110.38, -101.96) * mm, "radius": 30 * mm});
            skSolve(sketch);
        }
        {
            var Q0;
            Q0=makeQuery(id+"F2.imprint","IMPRINT",FACE,{"disambiguationData":[TD([[makeQuery(id+"F2.imprint","IMPRINT",EDGE,{"derivedFrom":sQuery(id+"F2.wireOp",EDGE,"E1")}),-1.0]])]});
            var Q1;
            Q1=makeQuery(id+"F2.imprint","IMPRINT",FACE,{"disambiguationData":[TD([[makeQuery(id+"F2.imprint","IMPRINT",EDGE,{"derivedFrom":sQuery(id+"F2.wireOp",EDGE,"E327")}),-1.0]])]});
            var Q2;
            Q2=makeQuery(id+"F2.imprint","IMPRINT",FACE,{"disambiguationData":[TD([[makeQuery(id+"F2.imprint","IMPRINT",EDGE,{"derivedFrom":sQuery(id+"F2.wireOp",EDGE,"E343")}),1.0]])]});
            var Q3;
            Q3=makeQuery(id+"F2.imprint","IMPRINT",FACE,{"disambiguationData":[TD([[makeQuery(id+"F2.imprint","IMPRINT",EDGE,{"derivedFrom":sQuery(id+"F2.wireOp",EDGE,"E345")}),1.0]])]});
            var Q4;
            Q4=makeQuery(id+"F2.imprint","IMPRINT",FACE,{"disambiguationData":[TD([[makeQuery(id+"F2.imprint","IMPRINT",EDGE,{"derivedFrom":sQuery(id+"F2.wireOp",EDGE,"E341")}),1.0]])]});
            var Q5;
            Q5=makeQuery(id+"F2.imprint","IMPRINT",FACE,{"disambiguationData":[TD([[makeQuery(id+"F2.imprint","IMPRINT",EDGE,{"derivedFrom":sQuery(id+"F2.wireOp",EDGE,"E346")}),1.0]])]});
            var Q6;
            Q6=makeQuery(id+"F2.imprint","IMPRINT",FACE,{"disambiguationData":[TD([[makeQuery(id+"F2.imprint","IMPRINT",EDGE,{"derivedFrom":sQuery(id+"F2.wireOp",EDGE,"E344")}),1.0]])]});
            var Q7;
            Q7=makeQuery(id+"F2.imprint","IMPRINT",FACE,{"disambiguationData":[TD([[makeQuery(id+"F2.imprint","IMPRINT",EDGE,{"derivedFrom":sQuery(id+"F2.wireOp",EDGE,"E341")}),-1.0]])]});
            extrude(context, id + "F3", {"entities" : qUnion([Q0, Q1, Q2, Q3, Q4, Q5, Q6, Q7]), "depth" : 5 * mm, "offsetDistance" : 25 * mm});
        }
        {
            var Q0;
            Q0=makeQuery(id+"F2.imprint","IMPRINT",FACE,{"disambiguationData":[TD([[makeQuery(id+"F2.imprint","IMPRINT",EDGE,{"derivedFrom":sQuery(id+"F2.wireOp",EDGE,"E323")}),-1.0]])]});
            var Q1;
            Q1=makeQuery(id+"F2.imprint","IMPRINT",FACE,{"disambiguationData":[TD([[makeQuery(id+"F2.imprint","IMPRINT",EDGE,{"derivedFrom":sQuery(id+"F2.wireOp",EDGE,"E324")}),-1.0]])]});
            extrude(context, id + "F4", {"entities" : qUnion([Q0, Q1]), "operationType" : NewBodyOperationType.ADD, "depth" : 2 * mm, "offsetDistance" : 25 * mm});
        }
        {
            var Q0;
            Q0=makeQuery(id+"F2.imprint","IMPRINT",FACE,{"disambiguationData":[TD([[makeQuery(id+"F2.imprint","IMPRINT",EDGE,{"derivedFrom":sQuery(id+"F2.wireOp",EDGE,"E347")}),-1.0]])]});
            var Q1;
            Q1=makeQuery(id+"F2.imprint","IMPRINT",FACE,{"disambiguationData":[TD([[makeQuery(id+"F2.imprint","IMPRINT",EDGE,{"derivedFrom":sQuery(id+"F2.wireOp",EDGE,"E660")}),1.0]])]});
            var Q2;
            Q2=makeQuery(id+"F2.imprint","IMPRINT",FACE,{"disambiguationData":[TD([[makeQuery(id+"F2.imprint","IMPRINT",EDGE,{"derivedFrom":sQuery(id+"F2.wireOp",EDGE,"E655")}),1.0]])]});
            var Q3;
            Q3=makeQuery(id+"F2.imprint","IMPRINT",FACE,{"disambiguationData":[TD([[makeQuery(id+"F2.imprint","IMPRINT",EDGE,{"derivedFrom":sQuery(id+"F2.wireOp",EDGE,"E659")}),1.0]])]});
            var Q4;
            Q4=makeQuery(id+"F2.imprint","IMPRINT",FACE,{"disambiguationData":[TD([[makeQuery(id+"F2.imprint","IMPRINT",EDGE,{"derivedFrom":sQuery(id+"F2.wireOp",EDGE,"E657")}),1.0]])]});
            var Q5;
            Q5=makeQuery(id+"F2.imprint","IMPRINT",FACE,{"disambiguationData":[TD([[makeQuery(id+"F2.imprint","IMPRINT",EDGE,{"derivedFrom":sQuery(id+"F2.wireOp",EDGE,"E655")}),-1.0]])]});
            var Q6;
            Q6=makeQuery(id+"F2.imprint","IMPRINT",FACE,{"disambiguationData":[TD([[makeQuery(id+"F2.imprint","IMPRINT",EDGE,{"derivedFrom":sQuery(id+"F2.wireOp",EDGE,"E658")}),1.0]])]});
            extrude(context, id + "F5", {"entities" : qUnion([Q0, Q1, Q2, Q3, Q4, Q5, Q6]), "depth" : 3 * mm, "offsetDistance" : 25 * mm});
        }
        {
            var Q0;
            Q0=makeQuery(id+"F2.imprint","IMPRINT",FACE,{"disambiguationData":[TD([[makeQuery(id+"F2.imprint","IMPRINT",EDGE,{"derivedFrom":sQuery(id+"F2.wireOp",EDGE,"E661.bottom")}),-1.0]])]});
            extrude(context, id + "F6", {"entities" : qUnion([Q0]), "depth" : 50 * mm, "offsetDistance" : 25 * mm});
        }
        {
            var Q0;
            Q0=makeQuery(id+"F2.imprint","IMPRINT",FACE,{"disambiguationData":[TD([[makeQuery(id+"F2.imprint","IMPRINT",EDGE,{"derivedFrom":sQuery(id+"F2.wireOp",EDGE,"E662")}),1.0]])]});
            extrude(context, id + "F7", {"entities" : qUnion([Q0]), "depth" : 60 * mm, "offsetDistance" : 25 * mm});
        }
        {
            var Q0;
            Q0=makeQuery(id+"F2.imprint","IMPRINT",FACE,{"disambiguationData":[TD([[makeQuery(id+"F2.imprint","IMPRINT",EDGE,{"derivedFrom":sQuery(id+"F2.wireOp",EDGE,"E663.bottom")}),-1.0]])]});
            extrude(context, id + "F8", {"entities" : qUnion([Q0]), "depth" : 25 * mm, "offsetDistance" : 25 * mm});
        }
        {
            var Q0;
            Q0=makeQuery(id+"F2.imprint","IMPRINT",FACE,{"disambiguationData":[TD([[makeQuery(id+"F2.imprint","IMPRINT",EDGE,{"derivedFrom":sQuery(id+"F2.wireOp",EDGE,"E664.bottom")}),-1.0]])]});
            extrude(context, id + "F9", {"entities" : qUnion([Q0]), "depth" : 57 * mm, "offsetDistance" : 25 * mm});
        }
    });
